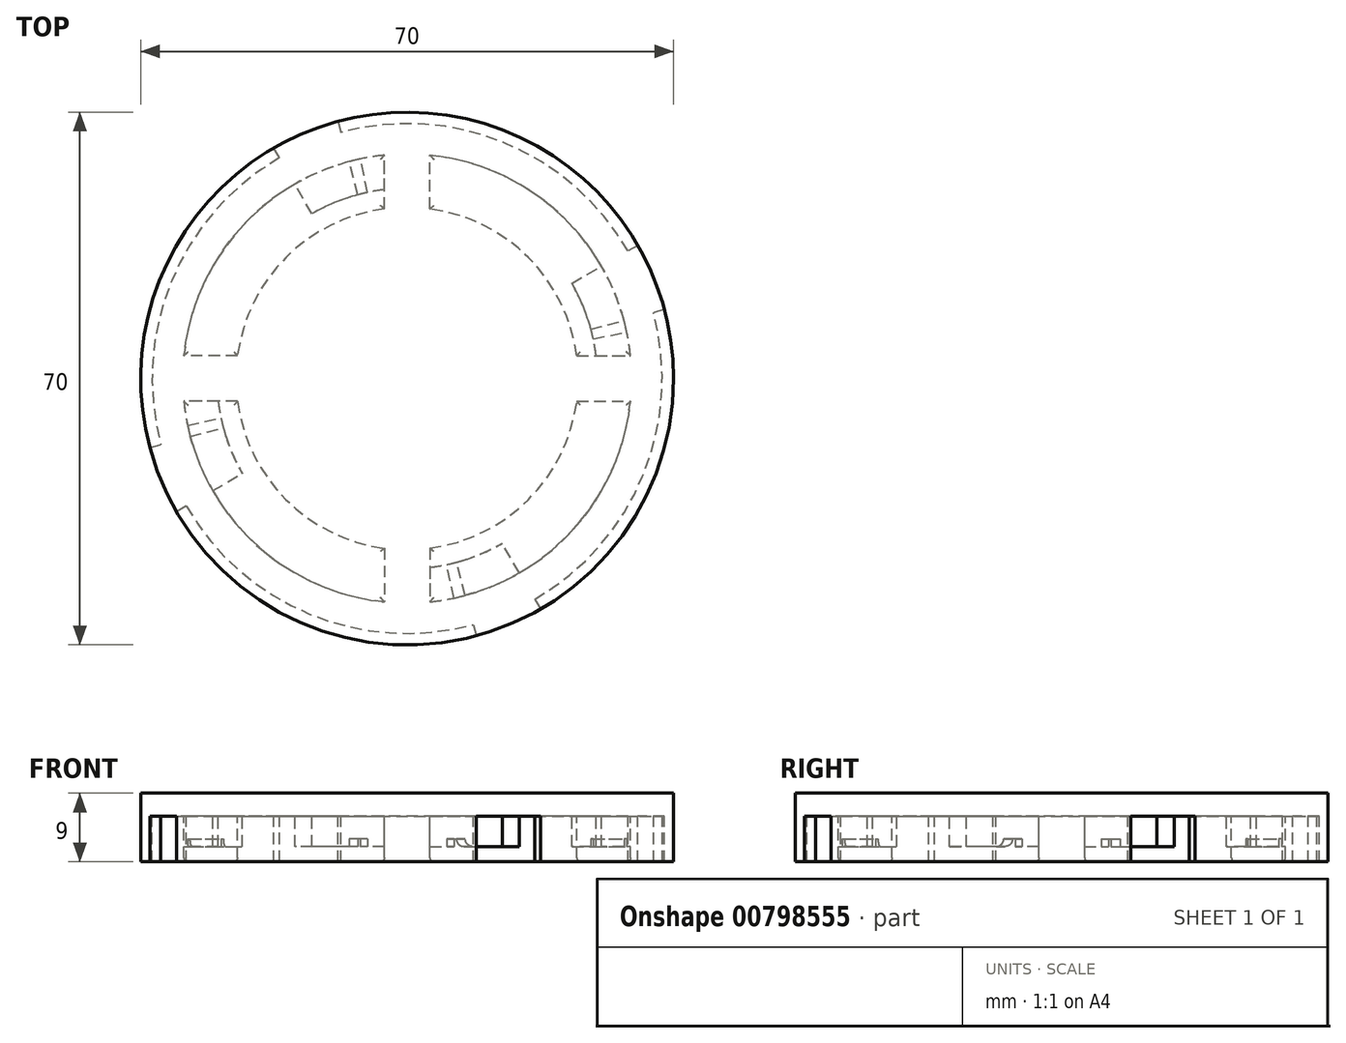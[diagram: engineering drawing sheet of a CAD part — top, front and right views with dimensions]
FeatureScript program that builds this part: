
annotation { "Feature Type Name" : "Feature", "Feature Type Description" : "" }
export const myFeature = defineFeature(function(context is Context, id is Id, definition is map)
    precondition{}
    {
        {
            var Q0;
            Q0=qCreatedBy(makeId("Top.planeOp"),FACE);
            var sketch = newSketch(context, id + "F0", { "sketchPlane" : qUnion([Q0])});
            skCircle(sketch, "E0", {"center": v(0, 0) * mm, "radius": 35 * mm});
            skCircle(sketch, "E1", {"center": v(0, 0) * mm, "radius": 29.5 * mm});
            skCircle(sketch, "E2", {"center": v(0, 0) * mm, "radius": 31 * mm});
            skCircle(sketch, "E3", {"center": v(0, 0) * mm, "radius": 33.5 * mm});
            skCircle(sketch, "E4", {"center": v(0, 0) * mm, "radius": 22.5 * mm});
            skLineSegment(sketch, "E5.bottom", {"start": v(-22.5, 3) * mm, "end": v(-29.5, 3) * mm});
            skLineSegment(sketch, "E5.top", {"start": v(-22.5, -3) * mm, "end": v(-29.5, -3) * mm});
            skLineSegment(sketch, "E5.left", {"start": v(-22.5, 3) * mm, "end": v(-22.5, -3) * mm});
            skLineSegment(sketch, "E5.right", {"start": v(-29.5, 3) * mm, "end": v(-29.5, -3) * mm});
            skPoint(sketch, "E5.middle", {"position": v(-26, 0) * mm});
            skLineSegment(sketch, "E6.bottom", {"start": v(-22.5, -3) * mm, "end": v(-21.5, -3) * mm});
            skLineSegment(sketch, "E6.top", {"start": v(-22.5, 3) * mm, "end": v(-21.5, 3) * mm});
            skLineSegment(sketch, "E6.left", {"start": v(-22.5, -3) * mm, "end": v(-22.5, 3) * mm});
            skLineSegment(sketch, "E6.right", {"start": v(-21.5, -3) * mm, "end": v(-21.5, 3) * mm});
            skPoint(sketch, "E6.middle", {"position": v(-22, 0) * mm});
            skLineSegment(sketch, "E7", {"start": v(-30.31, -17.5) * mm, "end": v(30.31, 17.5) * mm});
            skLineSegment(sketch, "E8", {"start": v(0, -35) * mm, "end": v(0, 35) * mm});
            skLineSegment(sketch, "E9.MirrorCS", {"start": v(21.5, -3) * mm, "end": v(21.5, 3) * mm});
            skLineSegment(sketch, "E10.MirrorCS", {"start": v(22.5, -3) * mm, "end": v(21.5, -3) * mm});
            skLineSegment(sketch, "E11.MirrorCS", {"start": v(22.5, -3) * mm, "end": v(29.5, -3) * mm});
            skLineSegment(sketch, "E12.MirrorCS", {"start": v(29.5, 3) * mm, "end": v(29.5, -3) * mm});
            skLineSegment(sketch, "E13.MirrorCS", {"start": v(22.5, 3) * mm, "end": v(29.5, 3) * mm});
            skLineSegment(sketch, "E14.MirrorCS", {"start": v(22.5, -3) * mm, "end": v(22.5, 3) * mm});
            skLineSegment(sketch, "E15.MirrorCS", {"start": v(22.5, 3) * mm, "end": v(21.5, 3) * mm});
            skLineSegment(sketch, "E16.bottom", {"start": v(3, -22.5) * mm, "end": v(-3, -22.5) * mm});
            skLineSegment(sketch, "E16.top", {"start": v(3, -29.5) * mm, "end": v(-3, -29.5) * mm});
            skLineSegment(sketch, "E16.left", {"start": v(3, -22.5) * mm, "end": v(3, -29.5) * mm});
            skLineSegment(sketch, "E16.right", {"start": v(-3, -22.5) * mm, "end": v(-3, -29.5) * mm});
            skPoint(sketch, "E16.middle", {"position": v(0, -26) * mm});
            skLineSegment(sketch, "E17.bottom", {"start": v(3, -21.5) * mm, "end": v(-3, -21.5) * mm});
            skLineSegment(sketch, "E17.left", {"start": v(3, -21.5) * mm, "end": v(3, -22.5) * mm});
            skLineSegment(sketch, "E17.right", {"start": v(-3, -21.5) * mm, "end": v(-3, -22.5) * mm});
            skPoint(sketch, "E17.middle", {"position": v(0, -22) * mm});
            skLineSegment(sketch, "E18", {"start": v(17.5, -30.31) * mm, "end": v(-17.5, 30.31) * mm});
            skLineSegment(sketch, "E19.bottom", {"start": v(3, 22.5) * mm, "end": v(-3, 22.5) * mm});
            skLineSegment(sketch, "E19.top", {"start": v(3, 29.5) * mm, "end": v(-3, 29.5) * mm});
            skLineSegment(sketch, "E19.left", {"start": v(3, 22.5) * mm, "end": v(3, 29.5) * mm});
            skLineSegment(sketch, "E19.right", {"start": v(-3, 22.5) * mm, "end": v(-3, 29.5) * mm});
            skPoint(sketch, "E19.middle", {"position": v(0, 26) * mm});
            skLineSegment(sketch, "E20.bottom", {"start": v(3, 21.5) * mm, "end": v(-3, 21.5) * mm});
            skLineSegment(sketch, "E20.left", {"start": v(3, 21.5) * mm, "end": v(3, 22.5) * mm});
            skLineSegment(sketch, "E20.right", {"start": v(-3, 21.5) * mm, "end": v(-3, 22.5) * mm});
            skPoint(sketch, "E20.middle", {"position": v(0, 22) * mm});
            skPoint(sketch, "E20.middle.positionSnap0", {"position": v(0, 29.5) * mm});
            skPoint(sketch, "E20.centerSnap0", {"position": v(0, 29.5) * mm});
            skCircle(sketch, "E21", {"center": v(0, 0) * mm, "radius": 25 * mm});
            skLineSegment(sketch, "E22", {"start": v(-35, 0) * mm, "end": v(35, 0) * mm});
            skPoint(sketch, "E23.startSnap0", {"position": v(3, -22) * mm});
            skLineSegment(sketch, "E24", {"start": v(9.06, -33.8) * mm, "end": v(-9.06, 33.8) * mm});
            skLineSegment(sketch, "E25", {"start": v(7.28, -34.24) * mm, "end": v(-7.28, 34.24) * mm});
            skLineSegment(sketch, "E26", {"start": v(-34.24, -7.28) * mm, "end": v(34.24, 7.28) * mm});
            skLineSegment(sketch, "E27", {"start": v(-33.8, -9.06) * mm, "end": v(33.8, 9.06) * mm});
            skSolve(sketch);
        }
        {
            var Q0;
            {var subQ0=sQuery(id+"F0.wireOp",EDGE,"E22");var subQ1=sQuery(id+"F0.wireOp",EDGE,"E0");var subQ2=makeQuery(id+"F0.imprint","INTERSECT",VERTEX,{"disambiguationData":[OD(1.0)],"derivedFrom":[subQ1,subQ0]});Q0=makeQuery(id+"F0.imprint","IMPRINT",FACE,{"disambiguationData":[TD([[makeQuery(id+"F0.imprint","IMPRINT",EDGE,{"disambiguationData":[TD([[subQ2,-1.0]])],"derivedFrom":subQ1}),1.0]])]});}
            var Q1;
            {var subQ0=sQuery(id+"F0.wireOp",EDGE,"E26");var subQ1=sQuery(id+"F0.wireOp",EDGE,"E0");var subQ2=makeQuery(id+"F0.imprint","INTERSECT",VERTEX,{"disambiguationData":[OD(1.0)],"derivedFrom":[subQ1,subQ0]});Q1=makeQuery(id+"F0.imprint","IMPRINT",FACE,{"disambiguationData":[TD([[makeQuery(id+"F0.imprint","IMPRINT",EDGE,{"disambiguationData":[TD([[subQ2,-1.0]])],"derivedFrom":subQ1}),1.0]])]});}
            var Q2;
            {var subQ0=sQuery(id+"F0.wireOp",EDGE,"E7");var subQ1=sQuery(id+"F0.wireOp",EDGE,"E0");var subQ2=makeQuery(id+"F0.imprint","INTERSECT",VERTEX,{"disambiguationData":[OD(1.0)],"derivedFrom":[subQ1,subQ0]});Q2=makeQuery(id+"F0.imprint","IMPRINT",FACE,{"disambiguationData":[TD([[makeQuery(id+"F0.imprint","IMPRINT",EDGE,{"disambiguationData":[TD([[subQ2,1.0]])],"derivedFrom":subQ1}),1.0]])]});}
            var Q3;
            {var subQ0=sQuery(id+"F0.wireOp",EDGE,"E7");var subQ1=sQuery(id+"F0.wireOp",EDGE,"E0");var subQ2=makeQuery(id+"F0.imprint","INTERSECT",VERTEX,{"disambiguationData":[OD(1.0)],"derivedFrom":[subQ1,subQ0]});Q3=makeQuery(id+"F0.imprint","IMPRINT",FACE,{"disambiguationData":[TD([[makeQuery(id+"F0.imprint","IMPRINT",EDGE,{"disambiguationData":[TD([[subQ2,-1.0]])],"derivedFrom":subQ1}),1.0]])]});}
            var Q4;
            {var subQ0=sQuery(id+"F0.wireOp",EDGE,"E8");var subQ1=sQuery(id+"F0.wireOp",EDGE,"E0");var subQ2=makeQuery(id+"F0.imprint","INTERSECT",VERTEX,{"disambiguationData":[OD(1.0)],"derivedFrom":[subQ1,subQ0]});Q4=makeQuery(id+"F0.imprint","IMPRINT",FACE,{"disambiguationData":[TD([[makeQuery(id+"F0.imprint","IMPRINT",EDGE,{"disambiguationData":[TD([[subQ2,-1.0]])],"derivedFrom":subQ1}),1.0]])]});}
            var Q5;
            {var subQ0=sQuery(id+"F0.wireOp",EDGE,"E24");var subQ1=sQuery(id+"F0.wireOp",EDGE,"E0");var subQ2=makeQuery(id+"F0.imprint","INTERSECT",VERTEX,{"disambiguationData":[OD(1.0)],"derivedFrom":[subQ1,subQ0]});Q5=makeQuery(id+"F0.imprint","IMPRINT",FACE,{"disambiguationData":[TD([[makeQuery(id+"F0.imprint","IMPRINT",EDGE,{"disambiguationData":[TD([[subQ2,1.0]])],"derivedFrom":subQ1}),1.0]])]});}
            var Q6;
            {var subQ0=sQuery(id+"F0.wireOp",EDGE,"E18");var subQ1=sQuery(id+"F0.wireOp",EDGE,"E0");var subQ2=makeQuery(id+"F0.imprint","INTERSECT",VERTEX,{"disambiguationData":[OD(1.0)],"derivedFrom":[subQ1,subQ0]});Q6=makeQuery(id+"F0.imprint","IMPRINT",FACE,{"disambiguationData":[TD([[makeQuery(id+"F0.imprint","IMPRINT",EDGE,{"disambiguationData":[TD([[subQ2,1.0]])],"derivedFrom":subQ1}),1.0]])]});}
            var Q7;
            {var subQ0=sQuery(id+"F0.wireOp",EDGE,"E18");var subQ1=sQuery(id+"F0.wireOp",EDGE,"E0");var subQ2=makeQuery(id+"F0.imprint","INTERSECT",VERTEX,{"disambiguationData":[OD(1.0)],"derivedFrom":[subQ1,subQ0]});Q7=makeQuery(id+"F0.imprint","IMPRINT",FACE,{"disambiguationData":[TD([[makeQuery(id+"F0.imprint","IMPRINT",EDGE,{"disambiguationData":[TD([[subQ2,-1.0]])],"derivedFrom":subQ1}),1.0]])]});}
            var Q8;
            {var subQ0=sQuery(id+"F0.wireOp",EDGE,"E22");var subQ1=sQuery(id+"F0.wireOp",EDGE,"E0");var subQ2=makeQuery(id+"F0.imprint","INTERSECT",VERTEX,{"disambiguationData":[OD(0.0)],"derivedFrom":[subQ1,subQ0]});Q8=makeQuery(id+"F0.imprint","IMPRINT",FACE,{"disambiguationData":[TD([[makeQuery(id+"F0.imprint","IMPRINT",EDGE,{"disambiguationData":[TD([[subQ2,-1.0]])],"derivedFrom":subQ1}),1.0]])]});}
            var Q9;
            {var subQ0=sQuery(id+"F0.wireOp",EDGE,"E26");var subQ1=sQuery(id+"F0.wireOp",EDGE,"E0");var subQ2=makeQuery(id+"F0.imprint","INTERSECT",VERTEX,{"disambiguationData":[OD(0.0)],"derivedFrom":[subQ1,subQ0]});Q9=makeQuery(id+"F0.imprint","IMPRINT",FACE,{"disambiguationData":[TD([[makeQuery(id+"F0.imprint","IMPRINT",EDGE,{"disambiguationData":[TD([[subQ2,-1.0]])],"derivedFrom":subQ1}),1.0]])]});}
            var Q10;
            {var subQ0=sQuery(id+"F0.wireOp",EDGE,"E7");var subQ1=sQuery(id+"F0.wireOp",EDGE,"E0");var subQ2=makeQuery(id+"F0.imprint","INTERSECT",VERTEX,{"disambiguationData":[OD(0.0)],"derivedFrom":[subQ1,subQ0]});Q10=makeQuery(id+"F0.imprint","IMPRINT",FACE,{"disambiguationData":[TD([[makeQuery(id+"F0.imprint","IMPRINT",EDGE,{"disambiguationData":[TD([[subQ2,1.0]])],"derivedFrom":subQ1}),1.0]])]});}
            var Q11;
            {var subQ0=sQuery(id+"F0.wireOp",EDGE,"E7");var subQ1=sQuery(id+"F0.wireOp",EDGE,"E0");var subQ2=makeQuery(id+"F0.imprint","INTERSECT",VERTEX,{"disambiguationData":[OD(0.0)],"derivedFrom":[subQ1,subQ0]});Q11=makeQuery(id+"F0.imprint","IMPRINT",FACE,{"disambiguationData":[TD([[makeQuery(id+"F0.imprint","IMPRINT",EDGE,{"disambiguationData":[TD([[subQ2,-1.0]])],"derivedFrom":subQ1}),1.0]])]});}
            var Q12;
            {var subQ0=sQuery(id+"F0.wireOp",EDGE,"E8");var subQ1=sQuery(id+"F0.wireOp",EDGE,"E0");var subQ2=makeQuery(id+"F0.imprint","INTERSECT",VERTEX,{"disambiguationData":[OD(0.0)],"derivedFrom":[subQ1,subQ0]});Q12=makeQuery(id+"F0.imprint","IMPRINT",FACE,{"disambiguationData":[TD([[makeQuery(id+"F0.imprint","IMPRINT",EDGE,{"disambiguationData":[TD([[subQ2,-1.0]])],"derivedFrom":subQ1}),1.0]])]});}
            var Q13;
            {var subQ0=sQuery(id+"F0.wireOp",EDGE,"E24");var subQ1=sQuery(id+"F0.wireOp",EDGE,"E0");var subQ2=makeQuery(id+"F0.imprint","INTERSECT",VERTEX,{"disambiguationData":[OD(0.0)],"derivedFrom":[subQ1,subQ0]});Q13=makeQuery(id+"F0.imprint","IMPRINT",FACE,{"disambiguationData":[TD([[makeQuery(id+"F0.imprint","IMPRINT",EDGE,{"disambiguationData":[TD([[subQ2,1.0]])],"derivedFrom":subQ1}),1.0]])]});}
            var Q14;
            {var subQ0=sQuery(id+"F0.wireOp",EDGE,"E18");var subQ1=sQuery(id+"F0.wireOp",EDGE,"E0");var subQ2=makeQuery(id+"F0.imprint","INTERSECT",VERTEX,{"disambiguationData":[OD(0.0)],"derivedFrom":[subQ1,subQ0]});Q14=makeQuery(id+"F0.imprint","IMPRINT",FACE,{"disambiguationData":[TD([[makeQuery(id+"F0.imprint","IMPRINT",EDGE,{"disambiguationData":[TD([[subQ2,1.0]])],"derivedFrom":subQ1}),1.0]])]});}
            var Q15;
            {var subQ0=sQuery(id+"F0.wireOp",EDGE,"E18");var subQ1=sQuery(id+"F0.wireOp",EDGE,"E0");var subQ2=makeQuery(id+"F0.imprint","INTERSECT",VERTEX,{"disambiguationData":[OD(0.0)],"derivedFrom":[subQ1,subQ0]});Q15=makeQuery(id+"F0.imprint","IMPRINT",FACE,{"disambiguationData":[TD([[makeQuery(id+"F0.imprint","IMPRINT",EDGE,{"disambiguationData":[TD([[subQ2,-1.0]])],"derivedFrom":subQ1}),1.0]])]});}
            var Q16;
            {var subQ0=sQuery(id+"F0.wireOp",EDGE,"E18");var subQ1=sQuery(id+"F0.wireOp",EDGE,"E4");var subQ2=makeQuery(id+"F0.imprint","INTERSECT",VERTEX,{"disambiguationData":[OD(0.0)],"derivedFrom":[subQ1,subQ0]});Q16=makeQuery(id+"F0.imprint","IMPRINT",FACE,{"disambiguationData":[TD([[makeQuery(id+"F0.imprint","IMPRINT",EDGE,{"disambiguationData":[TD([[subQ2,-1.0]])],"derivedFrom":subQ1}),1.0]])]});}
            var Q17;
            {var subQ5=sQuery(id+"F0.wireOp",EDGE,"E6.bottom");var subQ6=sQuery(id+"F0.wireOp",EDGE,"E4");var subQ7=makeQuery(id+"F0.imprint","INTERSECT",VERTEX,{"derivedFrom":[subQ6,subQ5]});Q17=makeQuery(id+"F0.imprint","IMPRINT",FACE,{"disambiguationData":[TD([[makeQuery(id+"F0.imprint","IMPRINT",EDGE,{"disambiguationData":[TD([[subQ7,-1.0]])],"derivedFrom":subQ6}),1.0]])]});}
            var Q18;
            {var subQ0=sQuery(id+"F0.wireOp",EDGE,"E26");var subQ1=sQuery(id+"F0.wireOp",EDGE,"E2");var subQ2=makeQuery(id+"F0.imprint","INTERSECT",VERTEX,{"disambiguationData":[OD(0.0)],"derivedFrom":[subQ1,subQ0]});Q18=makeQuery(id+"F0.imprint","IMPRINT",FACE,{"disambiguationData":[TD([[makeQuery(id+"F0.imprint","IMPRINT",EDGE,{"disambiguationData":[TD([[subQ2,1.0]])],"derivedFrom":subQ1}),-1.0]])]});}
            var Q19;
            {var subQ0=sQuery(id+"F0.wireOp",EDGE,"E26");var subQ1=sQuery(id+"F0.wireOp",EDGE,"E2");var subQ2=makeQuery(id+"F0.imprint","INTERSECT",VERTEX,{"disambiguationData":[OD(0.0)],"derivedFrom":[subQ1,subQ0]});Q19=makeQuery(id+"F0.imprint","IMPRINT",FACE,{"disambiguationData":[TD([[makeQuery(id+"F0.imprint","IMPRINT",EDGE,{"disambiguationData":[TD([[subQ2,-1.0]])],"derivedFrom":subQ1}),-1.0]])]});}
            var Q20;
            {var subQ0=sQuery(id+"F0.wireOp",EDGE,"E27");var subQ1=sQuery(id+"F0.wireOp",EDGE,"E2");var subQ2=makeQuery(id+"F0.imprint","INTERSECT",VERTEX,{"disambiguationData":[OD(0.0)],"derivedFrom":[subQ1,subQ0]});Q20=makeQuery(id+"F0.imprint","IMPRINT",FACE,{"disambiguationData":[TD([[makeQuery(id+"F0.imprint","IMPRINT",EDGE,{"disambiguationData":[TD([[subQ2,-1.0]])],"derivedFrom":subQ1}),-1.0]])]});}
            var Q21;
            {var subQ0=sQuery(id+"F0.wireOp",EDGE,"E7");var subQ1=sQuery(id+"F0.wireOp",EDGE,"E2");var subQ2=makeQuery(id+"F0.imprint","INTERSECT",VERTEX,{"disambiguationData":[OD(0.0)],"derivedFrom":[subQ1,subQ0]});Q21=makeQuery(id+"F0.imprint","IMPRINT",FACE,{"disambiguationData":[TD([[makeQuery(id+"F0.imprint","IMPRINT",EDGE,{"disambiguationData":[TD([[subQ2,-1.0]])],"derivedFrom":subQ1}),-1.0]])]});}
            var Q22;
            {var subQ0=sQuery(id+"F0.wireOp",EDGE,"E8");var subQ1=sQuery(id+"F0.wireOp",EDGE,"E2");var subQ2=makeQuery(id+"F0.imprint","INTERSECT",VERTEX,{"disambiguationData":[OD(0.0)],"derivedFrom":[subQ1,subQ0]});Q22=makeQuery(id+"F0.imprint","IMPRINT",FACE,{"disambiguationData":[TD([[makeQuery(id+"F0.imprint","IMPRINT",EDGE,{"disambiguationData":[TD([[subQ2,-1.0]])],"derivedFrom":subQ1}),-1.0]])]});}
            var Q23;
            {var subQ0=sQuery(id+"F0.wireOp",EDGE,"E25");var subQ1=sQuery(id+"F0.wireOp",EDGE,"E2");var subQ2=makeQuery(id+"F0.imprint","INTERSECT",VERTEX,{"disambiguationData":[OD(0.0)],"derivedFrom":[subQ1,subQ0]});Q23=makeQuery(id+"F0.imprint","IMPRINT",FACE,{"disambiguationData":[TD([[makeQuery(id+"F0.imprint","IMPRINT",EDGE,{"disambiguationData":[TD([[subQ2,-1.0]])],"derivedFrom":subQ1}),-1.0]])]});}
            var Q24;
            {var subQ0=sQuery(id+"F0.wireOp",EDGE,"E24");var subQ1=sQuery(id+"F0.wireOp",EDGE,"E2");var subQ2=makeQuery(id+"F0.imprint","INTERSECT",VERTEX,{"disambiguationData":[OD(0.0)],"derivedFrom":[subQ1,subQ0]});Q24=makeQuery(id+"F0.imprint","IMPRINT",FACE,{"disambiguationData":[TD([[makeQuery(id+"F0.imprint","IMPRINT",EDGE,{"disambiguationData":[TD([[subQ2,-1.0]])],"derivedFrom":subQ1}),-1.0]])]});}
            var Q25;
            {var subQ0=sQuery(id+"F0.wireOp",EDGE,"E18");var subQ1=sQuery(id+"F0.wireOp",EDGE,"E2");var subQ2=makeQuery(id+"F0.imprint","INTERSECT",VERTEX,{"disambiguationData":[OD(0.0)],"derivedFrom":[subQ1,subQ0]});Q25=makeQuery(id+"F0.imprint","IMPRINT",FACE,{"disambiguationData":[TD([[makeQuery(id+"F0.imprint","IMPRINT",EDGE,{"disambiguationData":[TD([[subQ2,-1.0]])],"derivedFrom":subQ1}),-1.0]])]});}
            var Q26;
            {var subQ0=sQuery(id+"F0.wireOp",EDGE,"E22");var subQ1=sQuery(id+"F0.wireOp",EDGE,"E2");var subQ2=makeQuery(id+"F0.imprint","INTERSECT",VERTEX,{"disambiguationData":[OD(1.0)],"derivedFrom":[subQ1,subQ0]});Q26=makeQuery(id+"F0.imprint","IMPRINT",FACE,{"disambiguationData":[TD([[makeQuery(id+"F0.imprint","IMPRINT",EDGE,{"disambiguationData":[TD([[subQ2,-1.0]])],"derivedFrom":subQ1}),-1.0]])]});}
            var Q27;
            {var subQ0=sQuery(id+"F0.wireOp",EDGE,"E26");var subQ1=sQuery(id+"F0.wireOp",EDGE,"E2");var subQ2=makeQuery(id+"F0.imprint","INTERSECT",VERTEX,{"disambiguationData":[OD(1.0)],"derivedFrom":[subQ1,subQ0]});Q27=makeQuery(id+"F0.imprint","IMPRINT",FACE,{"disambiguationData":[TD([[makeQuery(id+"F0.imprint","IMPRINT",EDGE,{"disambiguationData":[TD([[subQ2,-1.0]])],"derivedFrom":subQ1}),-1.0]])]});}
            var Q28;
            {var subQ0=sQuery(id+"F0.wireOp",EDGE,"E27");var subQ1=sQuery(id+"F0.wireOp",EDGE,"E2");var subQ2=makeQuery(id+"F0.imprint","INTERSECT",VERTEX,{"disambiguationData":[OD(1.0)],"derivedFrom":[subQ1,subQ0]});Q28=makeQuery(id+"F0.imprint","IMPRINT",FACE,{"disambiguationData":[TD([[makeQuery(id+"F0.imprint","IMPRINT",EDGE,{"disambiguationData":[TD([[subQ2,-1.0]])],"derivedFrom":subQ1}),-1.0]])]});}
            var Q29;
            {var subQ0=sQuery(id+"F0.wireOp",EDGE,"E7");var subQ1=sQuery(id+"F0.wireOp",EDGE,"E2");var subQ2=makeQuery(id+"F0.imprint","INTERSECT",VERTEX,{"disambiguationData":[OD(1.0)],"derivedFrom":[subQ1,subQ0]});Q29=makeQuery(id+"F0.imprint","IMPRINT",FACE,{"disambiguationData":[TD([[makeQuery(id+"F0.imprint","IMPRINT",EDGE,{"disambiguationData":[TD([[subQ2,-1.0]])],"derivedFrom":subQ1}),-1.0]])]});}
            var Q30;
            {var subQ0=sQuery(id+"F0.wireOp",EDGE,"E8");var subQ1=sQuery(id+"F0.wireOp",EDGE,"E2");var subQ2=makeQuery(id+"F0.imprint","INTERSECT",VERTEX,{"disambiguationData":[OD(1.0)],"derivedFrom":[subQ1,subQ0]});Q30=makeQuery(id+"F0.imprint","IMPRINT",FACE,{"disambiguationData":[TD([[makeQuery(id+"F0.imprint","IMPRINT",EDGE,{"disambiguationData":[TD([[subQ2,-1.0]])],"derivedFrom":subQ1}),-1.0]])]});}
            var Q31;
            {var subQ0=sQuery(id+"F0.wireOp",EDGE,"E25");var subQ1=sQuery(id+"F0.wireOp",EDGE,"E2");var subQ2=makeQuery(id+"F0.imprint","INTERSECT",VERTEX,{"disambiguationData":[OD(1.0)],"derivedFrom":[subQ1,subQ0]});Q31=makeQuery(id+"F0.imprint","IMPRINT",FACE,{"disambiguationData":[TD([[makeQuery(id+"F0.imprint","IMPRINT",EDGE,{"disambiguationData":[TD([[subQ2,-1.0]])],"derivedFrom":subQ1}),-1.0]])]});}
            var Q32;
            {var subQ0=sQuery(id+"F0.wireOp",EDGE,"E24");var subQ1=sQuery(id+"F0.wireOp",EDGE,"E2");var subQ2=makeQuery(id+"F0.imprint","INTERSECT",VERTEX,{"disambiguationData":[OD(1.0)],"derivedFrom":[subQ1,subQ0]});Q32=makeQuery(id+"F0.imprint","IMPRINT",FACE,{"disambiguationData":[TD([[makeQuery(id+"F0.imprint","IMPRINT",EDGE,{"disambiguationData":[TD([[subQ2,-1.0]])],"derivedFrom":subQ1}),-1.0]])]});}
            var Q33;
            {var subQ0=sQuery(id+"F0.wireOp",EDGE,"E22");var subQ1=sQuery(id+"F0.wireOp",EDGE,"E2");var subQ2=makeQuery(id+"F0.imprint","INTERSECT",VERTEX,{"disambiguationData":[OD(0.0)],"derivedFrom":[subQ1,subQ0]});Q33=makeQuery(id+"F0.imprint","IMPRINT",FACE,{"disambiguationData":[TD([[makeQuery(id+"F0.imprint","IMPRINT",EDGE,{"disambiguationData":[TD([[subQ2,1.0]])],"derivedFrom":subQ1}),-1.0]])]});}
            var Q34;
            {var subQ0=sQuery(id+"F0.wireOp",EDGE,"E27");var subQ1=sQuery(id+"F0.wireOp",EDGE,"E1");var subQ2=makeQuery(id+"F0.imprint","INTERSECT",VERTEX,{"disambiguationData":[OD(1.0)],"derivedFrom":[subQ1,subQ0]});Q34=makeQuery(id+"F0.imprint","IMPRINT",FACE,{"disambiguationData":[TD([[makeQuery(id+"F0.imprint","IMPRINT",EDGE,{"disambiguationData":[TD([[subQ2,-1.0]])],"derivedFrom":subQ1}),1.0]])]});}
            var Q35;
            {var subQ0=sQuery(id+"F0.wireOp",EDGE,"E15.MirrorCS");var subQ5=sQuery(id+"F0.wireOp",EDGE,"E9.MirrorCS");var subQ6=makeQuery(id+"F0.imprint","INTERSECT",VERTEX,{"derivedFrom":[subQ5,subQ0]});Q35=makeQuery(id+"F0.imprint","IMPRINT",FACE,{"disambiguationData":[TD([[makeQuery(id+"F0.imprint","IMPRINT",EDGE,{"disambiguationData":[TD([[subQ6,1.0]])],"derivedFrom":subQ5}),-1.0]])]});}
            var Q36;
            {var subQ0=sQuery(id+"F0.wireOp",EDGE,"E10.MirrorCS");var subQ5=sQuery(id+"F0.wireOp",EDGE,"E9.MirrorCS");var subQ7=makeQuery(id+"F0.imprint","INTERSECT",VERTEX,{"derivedFrom":[subQ5,subQ0]});Q36=makeQuery(id+"F0.imprint","IMPRINT",FACE,{"disambiguationData":[TD([[makeQuery(id+"F0.imprint","IMPRINT",EDGE,{"disambiguationData":[TD([[subQ7,-1.0]])],"derivedFrom":subQ5}),-1.0]])]});}
            var Q37;
            {var subQ5=sQuery(id+"F0.wireOp",EDGE,"E15.MirrorCS");var subQ7=sQuery(id+"F0.wireOp",EDGE,"E4");var subQ8=makeQuery(id+"F0.imprint","INTERSECT",VERTEX,{"derivedFrom":[subQ7,subQ5]});Q37=makeQuery(id+"F0.imprint","IMPRINT",FACE,{"disambiguationData":[TD([[makeQuery(id+"F0.imprint","IMPRINT",EDGE,{"disambiguationData":[TD([[subQ8,-1.0]])],"derivedFrom":subQ7}),1.0]])]});}
            var Q38;
            {var subQ0=sQuery(id+"F0.wireOp",EDGE,"E18");var subQ1=sQuery(id+"F0.wireOp",EDGE,"E4");var subQ2=makeQuery(id+"F0.imprint","INTERSECT",VERTEX,{"disambiguationData":[OD(1.0)],"derivedFrom":[subQ1,subQ0]});Q38=makeQuery(id+"F0.imprint","IMPRINT",FACE,{"disambiguationData":[TD([[makeQuery(id+"F0.imprint","IMPRINT",EDGE,{"disambiguationData":[TD([[subQ2,-1.0]])],"derivedFrom":subQ1}),1.0]])]});}
            var Q39;
            {var subQ0=sQuery(id+"F0.wireOp",EDGE,"E27");var subQ1=sQuery(id+"F0.wireOp",EDGE,"E1");var subQ2=makeQuery(id+"F0.imprint","INTERSECT",VERTEX,{"disambiguationData":[OD(0.0)],"derivedFrom":[subQ1,subQ0]});Q39=makeQuery(id+"F0.imprint","IMPRINT",FACE,{"disambiguationData":[TD([[makeQuery(id+"F0.imprint","IMPRINT",EDGE,{"disambiguationData":[TD([[subQ2,-1.0]])],"derivedFrom":subQ1}),1.0]])]});}
            var Q40;
            {var subQ0=sQuery(id+"F0.wireOp",EDGE,"E7");var subQ1=sQuery(id+"F0.wireOp",EDGE,"E1");var subQ2=makeQuery(id+"F0.imprint","INTERSECT",VERTEX,{"disambiguationData":[OD(0.0)],"derivedFrom":[subQ1,subQ0]});Q40=makeQuery(id+"F0.imprint","IMPRINT",FACE,{"disambiguationData":[TD([[makeQuery(id+"F0.imprint","IMPRINT",EDGE,{"disambiguationData":[TD([[subQ2,-1.0]])],"derivedFrom":subQ1}),1.0]])]});}
            var Q41;
            {var subQ0=sQuery(id+"F0.wireOp",EDGE,"E13.MirrorCS");var subQ1=sQuery(id+"F0.wireOp",EDGE,"E1");var subQ2=makeQuery(id+"F0.imprint","INTERSECT",VERTEX,{"derivedFrom":[subQ1,subQ0]});Q41=makeQuery(id+"F0.imprint","IMPRINT",FACE,{"disambiguationData":[TD([[makeQuery(id+"F0.imprint","IMPRINT",EDGE,{"disambiguationData":[TD([[subQ2,1.0]])],"derivedFrom":subQ0}),-1.0]])]});}
            var Q42;
            {var subQ0=sQuery(id+"F0.wireOp",EDGE,"E7");var subQ1=sQuery(id+"F0.wireOp",EDGE,"E1");var subQ2=makeQuery(id+"F0.imprint","INTERSECT",VERTEX,{"disambiguationData":[OD(1.0)],"derivedFrom":[subQ1,subQ0]});Q42=makeQuery(id+"F0.imprint","IMPRINT",FACE,{"disambiguationData":[TD([[makeQuery(id+"F0.imprint","IMPRINT",EDGE,{"disambiguationData":[TD([[subQ2,-1.0]])],"derivedFrom":subQ1}),1.0]])]});}
            var Q43;
            {var subQ0=sQuery(id+"F0.wireOp",EDGE,"E26");var subQ1=sQuery(id+"F0.wireOp",EDGE,"E1");var subQ2=makeQuery(id+"F0.imprint","INTERSECT",VERTEX,{"disambiguationData":[OD(0.0)],"derivedFrom":[subQ1,subQ0]});Q43=makeQuery(id+"F0.imprint","IMPRINT",FACE,{"disambiguationData":[TD([[makeQuery(id+"F0.imprint","IMPRINT",EDGE,{"disambiguationData":[TD([[subQ2,-1.0]])],"derivedFrom":subQ1}),-1.0]])]});}
            var Q44;
            {var subQ0=sQuery(id+"F0.wireOp",EDGE,"E27");var subQ1=sQuery(id+"F0.wireOp",EDGE,"E1");var subQ2=makeQuery(id+"F0.imprint","INTERSECT",VERTEX,{"disambiguationData":[OD(0.0)],"derivedFrom":[subQ1,subQ0]});Q44=makeQuery(id+"F0.imprint","IMPRINT",FACE,{"disambiguationData":[TD([[makeQuery(id+"F0.imprint","IMPRINT",EDGE,{"disambiguationData":[TD([[subQ2,-1.0]])],"derivedFrom":subQ1}),-1.0]])]});}
            var Q45;
            {var subQ0=sQuery(id+"F0.wireOp",EDGE,"E25");var subQ1=sQuery(id+"F0.wireOp",EDGE,"E1");var subQ2=makeQuery(id+"F0.imprint","INTERSECT",VERTEX,{"disambiguationData":[OD(0.0)],"derivedFrom":[subQ1,subQ0]});Q45=makeQuery(id+"F0.imprint","IMPRINT",FACE,{"disambiguationData":[TD([[makeQuery(id+"F0.imprint","IMPRINT",EDGE,{"disambiguationData":[TD([[subQ2,-1.0]])],"derivedFrom":subQ1}),-1.0]])]});}
            var Q46;
            {var subQ0=sQuery(id+"F0.wireOp",EDGE,"E24");var subQ1=sQuery(id+"F0.wireOp",EDGE,"E1");var subQ2=makeQuery(id+"F0.imprint","INTERSECT",VERTEX,{"disambiguationData":[OD(0.0)],"derivedFrom":[subQ1,subQ0]});Q46=makeQuery(id+"F0.imprint","IMPRINT",FACE,{"disambiguationData":[TD([[makeQuery(id+"F0.imprint","IMPRINT",EDGE,{"disambiguationData":[TD([[subQ2,-1.0]])],"derivedFrom":subQ1}),-1.0]])]});}
            var Q47;
            {var subQ0=sQuery(id+"F0.wireOp",EDGE,"E26");var subQ1=sQuery(id+"F0.wireOp",EDGE,"E1");var subQ2=makeQuery(id+"F0.imprint","INTERSECT",VERTEX,{"disambiguationData":[OD(1.0)],"derivedFrom":[subQ1,subQ0]});Q47=makeQuery(id+"F0.imprint","IMPRINT",FACE,{"disambiguationData":[TD([[makeQuery(id+"F0.imprint","IMPRINT",EDGE,{"disambiguationData":[TD([[subQ2,-1.0]])],"derivedFrom":subQ1}),-1.0]])]});}
            var Q48;
            {var subQ0=sQuery(id+"F0.wireOp",EDGE,"E27");var subQ1=sQuery(id+"F0.wireOp",EDGE,"E1");var subQ2=makeQuery(id+"F0.imprint","INTERSECT",VERTEX,{"disambiguationData":[OD(1.0)],"derivedFrom":[subQ1,subQ0]});Q48=makeQuery(id+"F0.imprint","IMPRINT",FACE,{"disambiguationData":[TD([[makeQuery(id+"F0.imprint","IMPRINT",EDGE,{"disambiguationData":[TD([[subQ2,-1.0]])],"derivedFrom":subQ1}),-1.0]])]});}
            var Q49;
            {var subQ0=sQuery(id+"F0.wireOp",EDGE,"E25");var subQ1=sQuery(id+"F0.wireOp",EDGE,"E1");var subQ2=makeQuery(id+"F0.imprint","INTERSECT",VERTEX,{"disambiguationData":[OD(1.0)],"derivedFrom":[subQ1,subQ0]});Q49=makeQuery(id+"F0.imprint","IMPRINT",FACE,{"disambiguationData":[TD([[makeQuery(id+"F0.imprint","IMPRINT",EDGE,{"disambiguationData":[TD([[subQ2,-1.0]])],"derivedFrom":subQ1}),-1.0]])]});}
            var Q50;
            {var subQ0=sQuery(id+"F0.wireOp",EDGE,"E24");var subQ1=sQuery(id+"F0.wireOp",EDGE,"E1");var subQ2=makeQuery(id+"F0.imprint","INTERSECT",VERTEX,{"disambiguationData":[OD(1.0)],"derivedFrom":[subQ1,subQ0]});Q50=makeQuery(id+"F0.imprint","IMPRINT",FACE,{"disambiguationData":[TD([[makeQuery(id+"F0.imprint","IMPRINT",EDGE,{"disambiguationData":[TD([[subQ2,-1.0]])],"derivedFrom":subQ1}),-1.0]])]});}
            var Q51;
            {var subQ0=sQuery(id+"F0.wireOp",EDGE,"E13.MirrorCS");var subQ3=sQuery(id+"F0.wireOp",EDGE,"E12.MirrorCS");var subQ5=makeQuery(id+"F0.imprint","INTERSECT",VERTEX,{"derivedFrom":[subQ3,subQ0]});Q51=makeQuery(id+"F0.imprint","IMPRINT",FACE,{"disambiguationData":[TD([[makeQuery(id+"F0.imprint","IMPRINT",EDGE,{"disambiguationData":[TD([[subQ5,1.0]])],"derivedFrom":subQ0}),-1.0]])]});}
            var Q52;
            {var subQ0=sQuery(id+"F0.wireOp",EDGE,"E6.top");var subQ5=sQuery(id+"F0.wireOp",EDGE,"E6.right");var subQ6=makeQuery(id+"F0.imprint","INTERSECT",VERTEX,{"derivedFrom":[subQ0,subQ5]});Q52=makeQuery(id+"F0.imprint","IMPRINT",FACE,{"disambiguationData":[TD([[makeQuery(id+"F0.imprint","IMPRINT",EDGE,{"disambiguationData":[TD([[subQ6,1.0]])],"derivedFrom":subQ0}),-1.0]])]});}
            var Q53;
            {var subQ0=sQuery(id+"F0.wireOp",EDGE,"E6.bottom");var subQ5=sQuery(id+"F0.wireOp",EDGE,"E6.right");var subQ6=makeQuery(id+"F0.imprint","INTERSECT",VERTEX,{"derivedFrom":[subQ0,subQ5]});Q53=makeQuery(id+"F0.imprint","IMPRINT",FACE,{"disambiguationData":[TD([[makeQuery(id+"F0.imprint","IMPRINT",EDGE,{"disambiguationData":[TD([[subQ6,1.0]])],"derivedFrom":subQ0}),1.0]])]});}
            var Q54;
            {var subQ0=sQuery(id+"F0.wireOp",EDGE,"E5.bottom");var subQ1=sQuery(id+"F0.wireOp",EDGE,"E1");var subQ2=makeQuery(id+"F0.imprint","INTERSECT",VERTEX,{"derivedFrom":[subQ1,subQ0]});Q54=makeQuery(id+"F0.imprint","IMPRINT",FACE,{"disambiguationData":[TD([[makeQuery(id+"F0.imprint","IMPRINT",EDGE,{"disambiguationData":[TD([[subQ2,1.0]])],"derivedFrom":subQ0}),1.0]])]});}
            var Q55;
            {var subQ0=sQuery(id+"F0.wireOp",EDGE,"E11.MirrorCS");var subQ3=sQuery(id+"F0.wireOp",EDGE,"E12.MirrorCS");var subQ5=makeQuery(id+"F0.imprint","INTERSECT",VERTEX,{"derivedFrom":[subQ0,subQ3]});Q55=makeQuery(id+"F0.imprint","IMPRINT",FACE,{"disambiguationData":[TD([[makeQuery(id+"F0.imprint","IMPRINT",EDGE,{"disambiguationData":[TD([[subQ5,1.0]])],"derivedFrom":subQ0}),1.0]])]});}
            var Q56;
            {var subQ0=sQuery(id+"F0.wireOp",EDGE,"E15.MirrorCS");var subQ1=sQuery(id+"F0.wireOp",EDGE,"E4");var subQ2=makeQuery(id+"F0.imprint","INTERSECT",VERTEX,{"derivedFrom":[subQ1,subQ0]});Q56=makeQuery(id+"F0.imprint","IMPRINT",FACE,{"disambiguationData":[TD([[makeQuery(id+"F0.imprint","IMPRINT",EDGE,{"disambiguationData":[TD([[subQ2,1.0]])],"derivedFrom":subQ1}),-1.0]])]});}
            var Q57;
            {var subQ0=sQuery(id+"F0.wireOp",EDGE,"E10.MirrorCS");var subQ1=sQuery(id+"F0.wireOp",EDGE,"E4");var subQ2=makeQuery(id+"F0.imprint","INTERSECT",VERTEX,{"derivedFrom":[subQ1,subQ0]});Q57=makeQuery(id+"F0.imprint","IMPRINT",FACE,{"disambiguationData":[TD([[makeQuery(id+"F0.imprint","IMPRINT",EDGE,{"disambiguationData":[TD([[subQ2,-1.0]])],"derivedFrom":subQ1}),-1.0]])]});}
            var Q58;
            {var subQ0=sQuery(id+"F0.wireOp",EDGE,"E5.bottom");var subQ3=sQuery(id+"F0.wireOp",EDGE,"E5.right");var subQ5=makeQuery(id+"F0.imprint","INTERSECT",VERTEX,{"derivedFrom":[subQ0,subQ3]});Q58=makeQuery(id+"F0.imprint","IMPRINT",FACE,{"disambiguationData":[TD([[makeQuery(id+"F0.imprint","IMPRINT",EDGE,{"disambiguationData":[TD([[subQ5,1.0]])],"derivedFrom":subQ0}),1.0]])]});}
            var Q59;
            {var subQ0=sQuery(id+"F0.wireOp",EDGE,"E6.bottom");var subQ1=sQuery(id+"F0.wireOp",EDGE,"E4");var subQ2=makeQuery(id+"F0.imprint","INTERSECT",VERTEX,{"derivedFrom":[subQ1,subQ0]});Q59=makeQuery(id+"F0.imprint","IMPRINT",FACE,{"disambiguationData":[TD([[makeQuery(id+"F0.imprint","IMPRINT",EDGE,{"disambiguationData":[TD([[subQ2,1.0]])],"derivedFrom":subQ1}),-1.0]])]});}
            var Q60;
            {var subQ0=sQuery(id+"F0.wireOp",EDGE,"E5.top");var subQ3=sQuery(id+"F0.wireOp",EDGE,"E5.right");var subQ5=makeQuery(id+"F0.imprint","INTERSECT",VERTEX,{"derivedFrom":[subQ0,subQ3]});Q60=makeQuery(id+"F0.imprint","IMPRINT",FACE,{"disambiguationData":[TD([[makeQuery(id+"F0.imprint","IMPRINT",EDGE,{"disambiguationData":[TD([[subQ5,1.0]])],"derivedFrom":subQ0}),-1.0]])]});}
            var Q61;
            {var subQ0=sQuery(id+"F0.wireOp",EDGE,"E6.top");var subQ1=sQuery(id+"F0.wireOp",EDGE,"E4");var subQ2=makeQuery(id+"F0.imprint","INTERSECT",VERTEX,{"derivedFrom":[subQ1,subQ0]});Q61=makeQuery(id+"F0.imprint","IMPRINT",FACE,{"disambiguationData":[TD([[makeQuery(id+"F0.imprint","IMPRINT",EDGE,{"disambiguationData":[TD([[subQ2,-1.0]])],"derivedFrom":subQ1}),-1.0]])]});}
            var Q62;
            {var subQ5=sQuery(id+"F0.wireOp",EDGE,"E7");var subQ6=sQuery(id+"F0.wireOp",EDGE,"E4");var subQ7=makeQuery(id+"F0.imprint","INTERSECT",VERTEX,{"disambiguationData":[OD(0.0)],"derivedFrom":[subQ6,subQ5]});Q62=makeQuery(id+"F0.imprint","IMPRINT",FACE,{"disambiguationData":[TD([[makeQuery(id+"F0.imprint","IMPRINT",EDGE,{"disambiguationData":[TD([[subQ7,-1.0]])],"derivedFrom":subQ6}),1.0]])]});}
            var Q63;
            {var subQ0=sQuery(id+"F0.wireOp",EDGE,"E20.right");var subQ3=sQuery(id+"F0.wireOp",EDGE,"E4");var subQ4=makeQuery(id+"F0.imprint","INTERSECT",VERTEX,{"derivedFrom":[subQ3,subQ0]});Q63=makeQuery(id+"F0.imprint","IMPRINT",FACE,{"disambiguationData":[TD([[makeQuery(id+"F0.imprint","IMPRINT",EDGE,{"disambiguationData":[TD([[subQ4,-1.0]])],"derivedFrom":subQ3}),1.0]])]});}
            var Q64;
            {var subQ0=sQuery(id+"F0.wireOp",EDGE,"E24");var subQ1=sQuery(id+"F0.wireOp",EDGE,"E1");var subQ2=makeQuery(id+"F0.imprint","INTERSECT",VERTEX,{"disambiguationData":[OD(1.0)],"derivedFrom":[subQ1,subQ0]});Q64=makeQuery(id+"F0.imprint","IMPRINT",FACE,{"disambiguationData":[TD([[makeQuery(id+"F0.imprint","IMPRINT",EDGE,{"disambiguationData":[TD([[subQ2,-1.0]])],"derivedFrom":subQ1}),1.0]])]});}
            var Q65;
            {var subQ0=sQuery(id+"F0.wireOp",EDGE,"E19.left");var subQ1=sQuery(id+"F0.wireOp",EDGE,"E1");var subQ2=makeQuery(id+"F0.imprint","INTERSECT",VERTEX,{"derivedFrom":[subQ1,subQ0]});Q65=makeQuery(id+"F0.imprint","IMPRINT",FACE,{"disambiguationData":[TD([[makeQuery(id+"F0.imprint","IMPRINT",EDGE,{"disambiguationData":[TD([[subQ2,1.0]])],"derivedFrom":subQ0}),1.0]])]});}
            var Q66;
            {var subQ0=sQuery(id+"F0.wireOp",EDGE,"E17.right");var subQ5=sQuery(id+"F0.wireOp",EDGE,"E17.bottom");var subQ7=makeQuery(id+"F0.imprint","INTERSECT",VERTEX,{"derivedFrom":[subQ5,subQ0]});Q66=makeQuery(id+"F0.imprint","IMPRINT",FACE,{"disambiguationData":[TD([[makeQuery(id+"F0.imprint","IMPRINT",EDGE,{"disambiguationData":[TD([[subQ7,1.0]])],"derivedFrom":subQ5}),1.0]])]});}
            var Q67;
            {var subQ0=sQuery(id+"F0.wireOp",EDGE,"E17.left");var subQ5=sQuery(id+"F0.wireOp",EDGE,"E17.bottom");var subQ7=makeQuery(id+"F0.imprint","INTERSECT",VERTEX,{"derivedFrom":[subQ5,subQ0]});Q67=makeQuery(id+"F0.imprint","IMPRINT",FACE,{"disambiguationData":[TD([[makeQuery(id+"F0.imprint","IMPRINT",EDGE,{"disambiguationData":[TD([[subQ7,-1.0]])],"derivedFrom":subQ5}),1.0]])]});}
            var Q68;
            {var subQ0=sQuery(id+"F0.wireOp",EDGE,"E18");var subQ1=sQuery(id+"F0.wireOp",EDGE,"E1");var subQ2=makeQuery(id+"F0.imprint","INTERSECT",VERTEX,{"disambiguationData":[OD(1.0)],"derivedFrom":[subQ1,subQ0]});Q68=makeQuery(id+"F0.imprint","IMPRINT",FACE,{"disambiguationData":[TD([[makeQuery(id+"F0.imprint","IMPRINT",EDGE,{"disambiguationData":[TD([[subQ2,-1.0]])],"derivedFrom":subQ1}),1.0]])]});}
            var Q69;
            {var subQ0=sQuery(id+"F0.wireOp",EDGE,"E18");var subQ1=sQuery(id+"F0.wireOp",EDGE,"E1");var subQ2=makeQuery(id+"F0.imprint","INTERSECT",VERTEX,{"disambiguationData":[OD(0.0)],"derivedFrom":[subQ1,subQ0]});Q69=makeQuery(id+"F0.imprint","IMPRINT",FACE,{"disambiguationData":[TD([[makeQuery(id+"F0.imprint","IMPRINT",EDGE,{"disambiguationData":[TD([[subQ2,-1.0]])],"derivedFrom":subQ1}),1.0]])]});}
            var Q70;
            {var subQ0=sQuery(id+"F0.wireOp",EDGE,"E16.right");var subQ1=sQuery(id+"F0.wireOp",EDGE,"E1");var subQ2=makeQuery(id+"F0.imprint","INTERSECT",VERTEX,{"derivedFrom":[subQ1,subQ0]});Q70=makeQuery(id+"F0.imprint","IMPRINT",FACE,{"disambiguationData":[TD([[makeQuery(id+"F0.imprint","IMPRINT",EDGE,{"disambiguationData":[TD([[subQ2,1.0]])],"derivedFrom":subQ0}),1.0]])]});}
            var Q71;
            {var subQ3=sQuery(id+"F0.wireOp",EDGE,"E7");var subQ7=sQuery(id+"F0.wireOp",EDGE,"E4");var subQ8=makeQuery(id+"F0.imprint","INTERSECT",VERTEX,{"disambiguationData":[OD(1.0)],"derivedFrom":[subQ7,subQ3]});Q71=makeQuery(id+"F0.imprint","IMPRINT",FACE,{"disambiguationData":[TD([[makeQuery(id+"F0.imprint","IMPRINT",EDGE,{"disambiguationData":[TD([[subQ8,-1.0]])],"derivedFrom":subQ7}),1.0]])]});}
            var Q72;
            {var subQ0=sQuery(id+"F0.wireOp",EDGE,"E17.left");var subQ7=sQuery(id+"F0.wireOp",EDGE,"E4");var subQ8=makeQuery(id+"F0.imprint","INTERSECT",VERTEX,{"derivedFrom":[subQ7,subQ0]});Q72=makeQuery(id+"F0.imprint","IMPRINT",FACE,{"disambiguationData":[TD([[makeQuery(id+"F0.imprint","IMPRINT",EDGE,{"disambiguationData":[TD([[subQ8,-1.0]])],"derivedFrom":subQ7}),1.0]])]});}
            var Q73;
            {var subQ0=sQuery(id+"F0.wireOp",EDGE,"E24");var subQ1=sQuery(id+"F0.wireOp",EDGE,"E1");var subQ2=makeQuery(id+"F0.imprint","INTERSECT",VERTEX,{"disambiguationData":[OD(0.0)],"derivedFrom":[subQ1,subQ0]});Q73=makeQuery(id+"F0.imprint","IMPRINT",FACE,{"disambiguationData":[TD([[makeQuery(id+"F0.imprint","IMPRINT",EDGE,{"disambiguationData":[TD([[subQ2,-1.0]])],"derivedFrom":subQ1}),1.0]])]});}
            var Q74;
            {var subQ0=sQuery(id+"F0.wireOp",EDGE,"E20.left");var subQ5=sQuery(id+"F0.wireOp",EDGE,"E20.bottom");var subQ7=makeQuery(id+"F0.imprint","INTERSECT",VERTEX,{"derivedFrom":[subQ5,subQ0]});Q74=makeQuery(id+"F0.imprint","IMPRINT",FACE,{"disambiguationData":[TD([[makeQuery(id+"F0.imprint","IMPRINT",EDGE,{"disambiguationData":[TD([[subQ7,-1.0]])],"derivedFrom":subQ5}),-1.0]])]});}
            var Q75;
            {var subQ0=sQuery(id+"F0.wireOp",EDGE,"E20.right");var subQ5=sQuery(id+"F0.wireOp",EDGE,"E20.bottom");var subQ7=makeQuery(id+"F0.imprint","INTERSECT",VERTEX,{"derivedFrom":[subQ5,subQ0]});Q75=makeQuery(id+"F0.imprint","IMPRINT",FACE,{"disambiguationData":[TD([[makeQuery(id+"F0.imprint","IMPRINT",EDGE,{"disambiguationData":[TD([[subQ7,1.0]])],"derivedFrom":subQ5}),-1.0]])]});}
            var Q76;
            {var subQ0=sQuery(id+"F0.wireOp",EDGE,"E16.right");var subQ3=sQuery(id+"F0.wireOp",EDGE,"E16.top");var subQ5=makeQuery(id+"F0.imprint","INTERSECT",VERTEX,{"derivedFrom":[subQ3,subQ0]});Q76=makeQuery(id+"F0.imprint","IMPRINT",FACE,{"disambiguationData":[TD([[makeQuery(id+"F0.imprint","IMPRINT",EDGE,{"disambiguationData":[TD([[subQ5,1.0]])],"derivedFrom":subQ0}),1.0]])]});}
            var Q77;
            {var subQ0=sQuery(id+"F0.wireOp",EDGE,"E16.left");var subQ3=sQuery(id+"F0.wireOp",EDGE,"E16.top");var subQ5=makeQuery(id+"F0.imprint","INTERSECT",VERTEX,{"derivedFrom":[subQ3,subQ0]});Q77=makeQuery(id+"F0.imprint","IMPRINT",FACE,{"disambiguationData":[TD([[makeQuery(id+"F0.imprint","IMPRINT",EDGE,{"disambiguationData":[TD([[subQ5,1.0]])],"derivedFrom":subQ0}),-1.0]])]});}
            var Q78;
            {var subQ0=sQuery(id+"F0.wireOp",EDGE,"E19.right");var subQ3=sQuery(id+"F0.wireOp",EDGE,"E19.top");var subQ5=makeQuery(id+"F0.imprint","INTERSECT",VERTEX,{"derivedFrom":[subQ3,subQ0]});Q78=makeQuery(id+"F0.imprint","IMPRINT",FACE,{"disambiguationData":[TD([[makeQuery(id+"F0.imprint","IMPRINT",EDGE,{"disambiguationData":[TD([[subQ5,1.0]])],"derivedFrom":subQ0}),-1.0]])]});}
            var Q79;
            {var subQ0=sQuery(id+"F0.wireOp",EDGE,"E19.left");var subQ3=sQuery(id+"F0.wireOp",EDGE,"E19.top");var subQ5=makeQuery(id+"F0.imprint","INTERSECT",VERTEX,{"derivedFrom":[subQ3,subQ0]});Q79=makeQuery(id+"F0.imprint","IMPRINT",FACE,{"disambiguationData":[TD([[makeQuery(id+"F0.imprint","IMPRINT",EDGE,{"disambiguationData":[TD([[subQ5,1.0]])],"derivedFrom":subQ0}),1.0]])]});}
            var Q80;
            {var subQ0=sQuery(id+"F0.wireOp",EDGE,"E17.left");var subQ1=sQuery(id+"F0.wireOp",EDGE,"E4");var subQ2=makeQuery(id+"F0.imprint","INTERSECT",VERTEX,{"derivedFrom":[subQ1,subQ0]});Q80=makeQuery(id+"F0.imprint","IMPRINT",FACE,{"disambiguationData":[TD([[makeQuery(id+"F0.imprint","IMPRINT",EDGE,{"disambiguationData":[TD([[subQ2,1.0]])],"derivedFrom":subQ1}),-1.0]])]});}
            var Q81;
            {var subQ0=sQuery(id+"F0.wireOp",EDGE,"E17.right");var subQ1=sQuery(id+"F0.wireOp",EDGE,"E4");var subQ2=makeQuery(id+"F0.imprint","INTERSECT",VERTEX,{"derivedFrom":[subQ1,subQ0]});Q81=makeQuery(id+"F0.imprint","IMPRINT",FACE,{"disambiguationData":[TD([[makeQuery(id+"F0.imprint","IMPRINT",EDGE,{"disambiguationData":[TD([[subQ2,-1.0]])],"derivedFrom":subQ1}),-1.0]])]});}
            var Q82;
            {var subQ0=sQuery(id+"F0.wireOp",EDGE,"E20.left");var subQ1=sQuery(id+"F0.wireOp",EDGE,"E4");var subQ2=makeQuery(id+"F0.imprint","INTERSECT",VERTEX,{"derivedFrom":[subQ1,subQ0]});Q82=makeQuery(id+"F0.imprint","IMPRINT",FACE,{"disambiguationData":[TD([[makeQuery(id+"F0.imprint","IMPRINT",EDGE,{"disambiguationData":[TD([[subQ2,-1.0]])],"derivedFrom":subQ1}),-1.0]])]});}
            var Q83;
            {var subQ0=sQuery(id+"F0.wireOp",EDGE,"E20.right");var subQ1=sQuery(id+"F0.wireOp",EDGE,"E4");var subQ2=makeQuery(id+"F0.imprint","INTERSECT",VERTEX,{"derivedFrom":[subQ1,subQ0]});Q83=makeQuery(id+"F0.imprint","IMPRINT",FACE,{"disambiguationData":[TD([[makeQuery(id+"F0.imprint","IMPRINT",EDGE,{"disambiguationData":[TD([[subQ2,1.0]])],"derivedFrom":subQ1}),-1.0]])]});}
            var Q84;
            {var subQ3=sQuery(id+"F0.wireOp",EDGE,"E4");var subQ7=sQuery(id+"F0.wireOp",EDGE,"E7");var subQ9=makeQuery(id+"F0.imprint","INTERSECT",VERTEX,{"disambiguationData":[OD(1.0)],"derivedFrom":[subQ3,subQ7]});Q84=makeQuery(id+"F0.imprint","IMPRINT",FACE,{"disambiguationData":[TD([[makeQuery(id+"F0.imprint","IMPRINT",EDGE,{"disambiguationData":[TD([[subQ9,-1.0]])],"derivedFrom":subQ3}),-1.0]])]});}
            var Q85;
            {var subQ5=sQuery(id+"F0.wireOp",EDGE,"E6.bottom");var subQ7=sQuery(id+"F0.wireOp",EDGE,"E4");var subQ8=makeQuery(id+"F0.imprint","INTERSECT",VERTEX,{"derivedFrom":[subQ7,subQ5]});Q85=makeQuery(id+"F0.imprint","IMPRINT",FACE,{"disambiguationData":[TD([[makeQuery(id+"F0.imprint","IMPRINT",EDGE,{"disambiguationData":[TD([[subQ8,-1.0]])],"derivedFrom":subQ7}),-1.0]])]});}
            var Q86;
            {var subQ3=sQuery(id+"F0.wireOp",EDGE,"E4");var subQ7=sQuery(id+"F0.wireOp",EDGE,"E18");var subQ8=makeQuery(id+"F0.imprint","INTERSECT",VERTEX,{"disambiguationData":[OD(0.0)],"derivedFrom":[subQ3,subQ7]});Q86=makeQuery(id+"F0.imprint","IMPRINT",FACE,{"disambiguationData":[TD([[makeQuery(id+"F0.imprint","IMPRINT",EDGE,{"disambiguationData":[TD([[subQ8,-1.0]])],"derivedFrom":subQ3}),-1.0]])]});}
            var Q87;
            {var subQ5=sQuery(id+"F0.wireOp",EDGE,"E20.right");var subQ7=sQuery(id+"F0.wireOp",EDGE,"E4");var subQ8=makeQuery(id+"F0.imprint","INTERSECT",VERTEX,{"derivedFrom":[subQ7,subQ5]});Q87=makeQuery(id+"F0.imprint","IMPRINT",FACE,{"disambiguationData":[TD([[makeQuery(id+"F0.imprint","IMPRINT",EDGE,{"disambiguationData":[TD([[subQ8,-1.0]])],"derivedFrom":subQ7}),-1.0]])]});}
            var Q88;
            {var subQ0=sQuery(id+"F0.wireOp",EDGE,"E21");var subQ1=sQuery(id+"F0.wireOp",EDGE,"E8");var subQ2=makeQuery(id+"F0.imprint","INTERSECT",VERTEX,{"disambiguationData":[OD(1.0)],"derivedFrom":[subQ1,subQ0]});Q88=makeQuery(id+"F0.imprint","IMPRINT",FACE,{"disambiguationData":[TD([[makeQuery(id+"F0.imprint","IMPRINT",EDGE,{"disambiguationData":[TD([[subQ2,1.0]])],"derivedFrom":subQ0}),1.0]])]});}
            var Q89;
            {var subQ3=sQuery(id+"F0.wireOp",EDGE,"E4");var subQ7=sQuery(id+"F0.wireOp",EDGE,"E7");var subQ8=makeQuery(id+"F0.imprint","INTERSECT",VERTEX,{"disambiguationData":[OD(0.0)],"derivedFrom":[subQ3,subQ7]});Q89=makeQuery(id+"F0.imprint","IMPRINT",FACE,{"disambiguationData":[TD([[makeQuery(id+"F0.imprint","IMPRINT",EDGE,{"disambiguationData":[TD([[subQ8,-1.0]])],"derivedFrom":subQ3}),-1.0]])]});}
            var Q90;
            {var subQ5=sQuery(id+"F0.wireOp",EDGE,"E15.MirrorCS");var subQ7=sQuery(id+"F0.wireOp",EDGE,"E4");var subQ8=makeQuery(id+"F0.imprint","INTERSECT",VERTEX,{"derivedFrom":[subQ7,subQ5]});Q90=makeQuery(id+"F0.imprint","IMPRINT",FACE,{"disambiguationData":[TD([[makeQuery(id+"F0.imprint","IMPRINT",EDGE,{"disambiguationData":[TD([[subQ8,-1.0]])],"derivedFrom":subQ7}),-1.0]])]});}
            var Q91;
            {var subQ5=sQuery(id+"F0.wireOp",EDGE,"E4");var subQ7=sQuery(id+"F0.wireOp",EDGE,"E18");var subQ8=makeQuery(id+"F0.imprint","INTERSECT",VERTEX,{"disambiguationData":[OD(1.0)],"derivedFrom":[subQ5,subQ7]});Q91=makeQuery(id+"F0.imprint","IMPRINT",FACE,{"disambiguationData":[TD([[makeQuery(id+"F0.imprint","IMPRINT",EDGE,{"disambiguationData":[TD([[subQ8,-1.0]])],"derivedFrom":subQ5}),-1.0]])]});}
            var Q92;
            {var subQ0=sQuery(id+"F0.wireOp",EDGE,"E21");var subQ1=sQuery(id+"F0.wireOp",EDGE,"E8");var subQ2=makeQuery(id+"F0.imprint","INTERSECT",VERTEX,{"disambiguationData":[OD(0.0)],"derivedFrom":[subQ1,subQ0]});Q92=makeQuery(id+"F0.imprint","IMPRINT",FACE,{"disambiguationData":[TD([[makeQuery(id+"F0.imprint","IMPRINT",EDGE,{"disambiguationData":[TD([[subQ2,-1.0]])],"derivedFrom":subQ0}),1.0]])]});}
            var Q93;
            {var subQ1=sQuery(id+"F0.wireOp",EDGE,"E11.MirrorCS");var subQ3=sQuery(id+"F0.wireOp",EDGE,"E21");var subQ4=makeQuery(id+"F0.imprint","INTERSECT",VERTEX,{"derivedFrom":[subQ1,subQ3]});Q93=makeQuery(id+"F0.imprint","IMPRINT",FACE,{"disambiguationData":[TD([[makeQuery(id+"F0.imprint","IMPRINT",EDGE,{"disambiguationData":[TD([[subQ4,-1.0]])],"derivedFrom":subQ3}),1.0]])]});}
            var Q94;
            {var subQ5=sQuery(id+"F0.wireOp",EDGE,"E17.left");var subQ7=sQuery(id+"F0.wireOp",EDGE,"E4");var subQ8=makeQuery(id+"F0.imprint","INTERSECT",VERTEX,{"derivedFrom":[subQ7,subQ5]});Q94=makeQuery(id+"F0.imprint","IMPRINT",FACE,{"disambiguationData":[TD([[makeQuery(id+"F0.imprint","IMPRINT",EDGE,{"disambiguationData":[TD([[subQ8,-1.0]])],"derivedFrom":subQ7}),-1.0]])]});}
            var Q95;
            {var subQ1=sQuery(id+"F0.wireOp",EDGE,"E5.bottom");var subQ3=sQuery(id+"F0.wireOp",EDGE,"E21");var subQ4=makeQuery(id+"F0.imprint","INTERSECT",VERTEX,{"derivedFrom":[subQ1,subQ3]});Q95=makeQuery(id+"F0.imprint","IMPRINT",FACE,{"disambiguationData":[TD([[makeQuery(id+"F0.imprint","IMPRINT",EDGE,{"disambiguationData":[TD([[subQ4,-1.0]])],"derivedFrom":subQ3}),1.0]])]});}
            var Q96;
            {var subQ0=sQuery(id+"F0.wireOp",EDGE,"E16.left");var subQ1=sQuery(id+"F0.wireOp",EDGE,"E1");var subQ2=makeQuery(id+"F0.imprint","INTERSECT",VERTEX,{"derivedFrom":[subQ1,subQ0]});Q96=makeQuery(id+"F0.imprint","IMPRINT",FACE,{"disambiguationData":[TD([[makeQuery(id+"F0.imprint","IMPRINT",EDGE,{"disambiguationData":[TD([[subQ2,1.0]])],"derivedFrom":subQ0}),-1.0]])]});}
            var Q97;
            {var subQ0=sQuery(id+"F0.wireOp",EDGE,"E21");var subQ1=sQuery(id+"F0.wireOp",EDGE,"E8");var subQ2=makeQuery(id+"F0.imprint","INTERSECT",VERTEX,{"disambiguationData":[OD(0.0)],"derivedFrom":[subQ1,subQ0]});Q97=makeQuery(id+"F0.imprint","IMPRINT",FACE,{"disambiguationData":[TD([[makeQuery(id+"F0.imprint","IMPRINT",EDGE,{"disambiguationData":[TD([[subQ2,1.0]])],"derivedFrom":subQ0}),1.0]])]});}
            var Q98;
            {var subQ0=sQuery(id+"F0.wireOp",EDGE,"E5.top");var subQ1=sQuery(id+"F0.wireOp",EDGE,"E1");var subQ2=makeQuery(id+"F0.imprint","INTERSECT",VERTEX,{"derivedFrom":[subQ1,subQ0]});Q98=makeQuery(id+"F0.imprint","IMPRINT",FACE,{"disambiguationData":[TD([[makeQuery(id+"F0.imprint","IMPRINT",EDGE,{"disambiguationData":[TD([[subQ2,1.0]])],"derivedFrom":subQ0}),-1.0]])]});}
            var Q99;
            {var subQ1=sQuery(id+"F0.wireOp",EDGE,"E5.top");var subQ3=sQuery(id+"F0.wireOp",EDGE,"E21");var subQ4=makeQuery(id+"F0.imprint","INTERSECT",VERTEX,{"derivedFrom":[subQ1,subQ3]});Q99=makeQuery(id+"F0.imprint","IMPRINT",FACE,{"disambiguationData":[TD([[makeQuery(id+"F0.imprint","IMPRINT",EDGE,{"disambiguationData":[TD([[subQ4,1.0]])],"derivedFrom":subQ3}),1.0]])]});}
            var Q100;
            {var subQ1=sQuery(id+"F0.wireOp",EDGE,"E13.MirrorCS");var subQ3=sQuery(id+"F0.wireOp",EDGE,"E21");var subQ4=makeQuery(id+"F0.imprint","INTERSECT",VERTEX,{"derivedFrom":[subQ1,subQ3]});Q100=makeQuery(id+"F0.imprint","IMPRINT",FACE,{"disambiguationData":[TD([[makeQuery(id+"F0.imprint","IMPRINT",EDGE,{"disambiguationData":[TD([[subQ4,1.0]])],"derivedFrom":subQ3}),1.0]])]});}
            var Q101;
            {var subQ0=sQuery(id+"F0.wireOp",EDGE,"E11.MirrorCS");var subQ1=sQuery(id+"F0.wireOp",EDGE,"E1");var subQ2=makeQuery(id+"F0.imprint","INTERSECT",VERTEX,{"derivedFrom":[subQ1,subQ0]});Q101=makeQuery(id+"F0.imprint","IMPRINT",FACE,{"disambiguationData":[TD([[makeQuery(id+"F0.imprint","IMPRINT",EDGE,{"disambiguationData":[TD([[subQ2,1.0]])],"derivedFrom":subQ0}),1.0]])]});}
            var Q102;
            {var subQ0=sQuery(id+"F0.wireOp",EDGE,"E19.right");var subQ1=sQuery(id+"F0.wireOp",EDGE,"E1");var subQ2=makeQuery(id+"F0.imprint","INTERSECT",VERTEX,{"derivedFrom":[subQ1,subQ0]});Q102=makeQuery(id+"F0.imprint","IMPRINT",FACE,{"disambiguationData":[TD([[makeQuery(id+"F0.imprint","IMPRINT",EDGE,{"disambiguationData":[TD([[subQ2,1.0]])],"derivedFrom":subQ0}),-1.0]])]});}
            var Q103;
            {var subQ0=sQuery(id+"F0.wireOp",EDGE,"E21");var subQ1=sQuery(id+"F0.wireOp",EDGE,"E8");var subQ2=makeQuery(id+"F0.imprint","INTERSECT",VERTEX,{"disambiguationData":[OD(1.0)],"derivedFrom":[subQ1,subQ0]});Q103=makeQuery(id+"F0.imprint","IMPRINT",FACE,{"disambiguationData":[TD([[makeQuery(id+"F0.imprint","IMPRINT",EDGE,{"disambiguationData":[TD([[subQ2,-1.0]])],"derivedFrom":subQ0}),1.0]])]});}
            var Q104;
            {var subQ0=sQuery(id+"F0.wireOp",EDGE,"E25");var subQ1=sQuery(id+"F0.wireOp",EDGE,"E4");var subQ2=makeQuery(id+"F0.imprint","INTERSECT",VERTEX,{"disambiguationData":[OD(0.0)],"derivedFrom":[subQ1,subQ0]});Q104=makeQuery(id+"F0.imprint","IMPRINT",FACE,{"disambiguationData":[TD([[makeQuery(id+"F0.imprint","IMPRINT",EDGE,{"disambiguationData":[TD([[subQ2,-1.0]])],"derivedFrom":subQ1}),1.0]])]});}
            var Q105;
            {var subQ0=sQuery(id+"F0.wireOp",EDGE,"E5.top");var subQ1=sQuery(id+"F0.wireOp",EDGE,"E1");var subQ2=makeQuery(id+"F0.imprint","INTERSECT",VERTEX,{"derivedFrom":[subQ1,subQ0]});Q105=makeQuery(id+"F0.imprint","IMPRINT",FACE,{"disambiguationData":[TD([[makeQuery(id+"F0.imprint","IMPRINT",EDGE,{"disambiguationData":[TD([[subQ2,-1.0]])],"derivedFrom":subQ1}),1.0]])]});}
            var Q106;
            {var subQ0=sQuery(id+"F0.wireOp",EDGE,"E26");var subQ1=sQuery(id+"F0.wireOp",EDGE,"E1");var subQ2=makeQuery(id+"F0.imprint","INTERSECT",VERTEX,{"disambiguationData":[OD(0.0)],"derivedFrom":[subQ1,subQ0]});Q106=makeQuery(id+"F0.imprint","IMPRINT",FACE,{"disambiguationData":[TD([[makeQuery(id+"F0.imprint","IMPRINT",EDGE,{"disambiguationData":[TD([[subQ2,-1.0]])],"derivedFrom":subQ1}),1.0]])]});}
            var Q107;
            {var subQ0=sQuery(id+"F0.wireOp",EDGE,"E26");var subQ1=sQuery(id+"F0.wireOp",EDGE,"E1");var subQ2=makeQuery(id+"F0.imprint","INTERSECT",VERTEX,{"disambiguationData":[OD(1.0)],"derivedFrom":[subQ1,subQ0]});Q107=makeQuery(id+"F0.imprint","IMPRINT",FACE,{"disambiguationData":[TD([[makeQuery(id+"F0.imprint","IMPRINT",EDGE,{"disambiguationData":[TD([[subQ2,-1.0]])],"derivedFrom":subQ1}),1.0]])]});}
            var Q108;
            {var subQ0=sQuery(id+"F0.wireOp",EDGE,"E16.left");var subQ1=sQuery(id+"F0.wireOp",EDGE,"E1");var subQ2=makeQuery(id+"F0.imprint","INTERSECT",VERTEX,{"derivedFrom":[subQ1,subQ0]});Q108=makeQuery(id+"F0.imprint","IMPRINT",FACE,{"disambiguationData":[TD([[makeQuery(id+"F0.imprint","IMPRINT",EDGE,{"disambiguationData":[TD([[subQ2,-1.0]])],"derivedFrom":subQ1}),1.0]])]});}
            var Q109;
            {var subQ0=sQuery(id+"F0.wireOp",EDGE,"E24");var subQ1=sQuery(id+"F0.wireOp",EDGE,"E4");var subQ2=makeQuery(id+"F0.imprint","INTERSECT",VERTEX,{"disambiguationData":[OD(0.0)],"derivedFrom":[subQ1,subQ0]});Q109=makeQuery(id+"F0.imprint","IMPRINT",FACE,{"disambiguationData":[TD([[makeQuery(id+"F0.imprint","IMPRINT",EDGE,{"disambiguationData":[TD([[subQ2,-1.0]])],"derivedFrom":subQ1}),1.0]])]});}
            var Q110;
            {var subQ0=sQuery(id+"F0.wireOp",EDGE,"E24");var subQ1=sQuery(id+"F0.wireOp",EDGE,"E4");var subQ2=makeQuery(id+"F0.imprint","INTERSECT",VERTEX,{"disambiguationData":[OD(0.0)],"derivedFrom":[subQ1,subQ0]});Q110=makeQuery(id+"F0.imprint","IMPRINT",FACE,{"disambiguationData":[TD([[makeQuery(id+"F0.imprint","IMPRINT",EDGE,{"disambiguationData":[TD([[subQ2,-1.0]])],"derivedFrom":subQ1}),-1.0]])]});}
            var Q111;
            {var subQ0=sQuery(id+"F0.wireOp",EDGE,"E27");var subQ1=sQuery(id+"F0.wireOp",EDGE,"E4");var subQ2=makeQuery(id+"F0.imprint","INTERSECT",VERTEX,{"disambiguationData":[OD(0.0)],"derivedFrom":[subQ1,subQ0]});Q111=makeQuery(id+"F0.imprint","IMPRINT",FACE,{"disambiguationData":[TD([[makeQuery(id+"F0.imprint","IMPRINT",EDGE,{"disambiguationData":[TD([[subQ2,-1.0]])],"derivedFrom":subQ1}),1.0]])]});}
            var Q112;
            {var subQ0=sQuery(id+"F0.wireOp",EDGE,"E25");var subQ1=sQuery(id+"F0.wireOp",EDGE,"E1");var subQ2=makeQuery(id+"F0.imprint","INTERSECT",VERTEX,{"disambiguationData":[OD(0.0)],"derivedFrom":[subQ1,subQ0]});Q112=makeQuery(id+"F0.imprint","IMPRINT",FACE,{"disambiguationData":[TD([[makeQuery(id+"F0.imprint","IMPRINT",EDGE,{"disambiguationData":[TD([[subQ2,-1.0]])],"derivedFrom":subQ1}),1.0]])]});}
            var Q113;
            {var subQ0=sQuery(id+"F0.wireOp",EDGE,"E7");var subQ1=sQuery(id+"F0.wireOp",EDGE,"E1");var subQ2=makeQuery(id+"F0.imprint","INTERSECT",VERTEX,{"disambiguationData":[OD(1.0)],"derivedFrom":[subQ1,subQ0]});Q113=makeQuery(id+"F0.imprint","IMPRINT",FACE,{"disambiguationData":[TD([[makeQuery(id+"F0.imprint","IMPRINT",EDGE,{"disambiguationData":[TD([[subQ2,-1.0]])],"derivedFrom":subQ1}),-1.0]])]});}
            var Q114;
            {var subQ0=sQuery(id+"F0.wireOp",EDGE,"E27");var subQ1=sQuery(id+"F0.wireOp",EDGE,"E4");var subQ2=makeQuery(id+"F0.imprint","INTERSECT",VERTEX,{"disambiguationData":[OD(1.0)],"derivedFrom":[subQ1,subQ0]});Q114=makeQuery(id+"F0.imprint","IMPRINT",FACE,{"disambiguationData":[TD([[makeQuery(id+"F0.imprint","IMPRINT",EDGE,{"disambiguationData":[TD([[subQ2,-1.0]])],"derivedFrom":subQ1}),-1.0]])]});}
            var Q115;
            {var subQ0=sQuery(id+"F0.wireOp",EDGE,"E26");var subQ1=sQuery(id+"F0.wireOp",EDGE,"E4");var subQ2=makeQuery(id+"F0.imprint","INTERSECT",VERTEX,{"disambiguationData":[OD(0.0)],"derivedFrom":[subQ1,subQ0]});Q115=makeQuery(id+"F0.imprint","IMPRINT",FACE,{"disambiguationData":[TD([[makeQuery(id+"F0.imprint","IMPRINT",EDGE,{"disambiguationData":[TD([[subQ2,-1.0]])],"derivedFrom":subQ1}),1.0]])]});}
            var Q116;
            {var subQ4=sQuery(id+"F0.wireOp",EDGE,"E1");var subQ8=sQuery(id+"F0.wireOp",EDGE,"E19.right");var subQ10=makeQuery(id+"F0.imprint","INTERSECT",VERTEX,{"derivedFrom":[subQ4,subQ8]});Q116=makeQuery(id+"F0.imprint","IMPRINT",FACE,{"disambiguationData":[TD([[makeQuery(id+"F0.imprint","IMPRINT",EDGE,{"disambiguationData":[TD([[subQ10,-1.0]])],"derivedFrom":subQ4}),-1.0]])]});}
            var Q117;
            {var subQ1=sQuery(id+"F0.wireOp",EDGE,"E5.top");var subQ3=sQuery(id+"F0.wireOp",EDGE,"E1");var subQ4=makeQuery(id+"F0.imprint","INTERSECT",VERTEX,{"derivedFrom":[subQ3,subQ1]});Q117=makeQuery(id+"F0.imprint","IMPRINT",FACE,{"disambiguationData":[TD([[makeQuery(id+"F0.imprint","IMPRINT",EDGE,{"disambiguationData":[TD([[subQ4,-1.0]])],"derivedFrom":subQ3}),-1.0]])]});}
            var Q118;
            {var subQ0=sQuery(id+"F0.wireOp",EDGE,"E25");var subQ1=sQuery(id+"F0.wireOp",EDGE,"E4");var subQ2=makeQuery(id+"F0.imprint","INTERSECT",VERTEX,{"disambiguationData":[OD(1.0)],"derivedFrom":[subQ1,subQ0]});Q118=makeQuery(id+"F0.imprint","IMPRINT",FACE,{"disambiguationData":[TD([[makeQuery(id+"F0.imprint","IMPRINT",EDGE,{"disambiguationData":[TD([[subQ2,-1.0]])],"derivedFrom":subQ1}),1.0]])]});}
            var Q119;
            {var subQ4=sQuery(id+"F0.wireOp",EDGE,"E1");var subQ9=sQuery(id+"F0.wireOp",EDGE,"E18");var subQ11=makeQuery(id+"F0.imprint","INTERSECT",VERTEX,{"disambiguationData":[OD(1.0)],"derivedFrom":[subQ4,subQ9]});Q119=makeQuery(id+"F0.imprint","IMPRINT",FACE,{"disambiguationData":[TD([[makeQuery(id+"F0.imprint","IMPRINT",EDGE,{"disambiguationData":[TD([[subQ11,-1.0]])],"derivedFrom":subQ4}),-1.0]])]});}
            var Q120;
            {var subQ0=sQuery(id+"F0.wireOp",EDGE,"E26");var subQ1=sQuery(id+"F0.wireOp",EDGE,"E4");var subQ2=makeQuery(id+"F0.imprint","INTERSECT",VERTEX,{"disambiguationData":[OD(1.0)],"derivedFrom":[subQ1,subQ0]});Q120=makeQuery(id+"F0.imprint","IMPRINT",FACE,{"disambiguationData":[TD([[makeQuery(id+"F0.imprint","IMPRINT",EDGE,{"disambiguationData":[TD([[subQ2,-1.0]])],"derivedFrom":subQ1}),-1.0]])]});}
            var Q121;
            {var subQ0=sQuery(id+"F0.wireOp",EDGE,"E7");var subQ1=sQuery(id+"F0.wireOp",EDGE,"E1");var subQ2=makeQuery(id+"F0.imprint","INTERSECT",VERTEX,{"disambiguationData":[OD(0.0)],"derivedFrom":[subQ1,subQ0]});Q121=makeQuery(id+"F0.imprint","IMPRINT",FACE,{"disambiguationData":[TD([[makeQuery(id+"F0.imprint","IMPRINT",EDGE,{"disambiguationData":[TD([[subQ2,-1.0]])],"derivedFrom":subQ1}),-1.0]])]});}
            var Q122;
            {var subQ0=sQuery(id+"F0.wireOp",EDGE,"E25");var subQ1=sQuery(id+"F0.wireOp",EDGE,"E4");var subQ2=makeQuery(id+"F0.imprint","INTERSECT",VERTEX,{"disambiguationData":[OD(0.0)],"derivedFrom":[subQ1,subQ0]});Q122=makeQuery(id+"F0.imprint","IMPRINT",FACE,{"disambiguationData":[TD([[makeQuery(id+"F0.imprint","IMPRINT",EDGE,{"disambiguationData":[TD([[subQ2,-1.0]])],"derivedFrom":subQ1}),-1.0]])]});}
            var Q123;
            {var subQ0=sQuery(id+"F0.wireOp",EDGE,"E19.right");var subQ1=sQuery(id+"F0.wireOp",EDGE,"E1");var subQ2=makeQuery(id+"F0.imprint","INTERSECT",VERTEX,{"derivedFrom":[subQ1,subQ0]});Q123=makeQuery(id+"F0.imprint","IMPRINT",FACE,{"disambiguationData":[TD([[makeQuery(id+"F0.imprint","IMPRINT",EDGE,{"disambiguationData":[TD([[subQ2,-1.0]])],"derivedFrom":subQ1}),1.0]])]});}
            var Q124;
            {var subQ0=sQuery(id+"F0.wireOp",EDGE,"E27");var subQ1=sQuery(id+"F0.wireOp",EDGE,"E4");var subQ2=makeQuery(id+"F0.imprint","INTERSECT",VERTEX,{"disambiguationData":[OD(0.0)],"derivedFrom":[subQ1,subQ0]});Q124=makeQuery(id+"F0.imprint","IMPRINT",FACE,{"disambiguationData":[TD([[makeQuery(id+"F0.imprint","IMPRINT",EDGE,{"disambiguationData":[TD([[subQ2,-1.0]])],"derivedFrom":subQ1}),-1.0]])]});}
            var Q125;
            {var subQ0=sQuery(id+"F0.wireOp",EDGE,"E24");var subQ1=sQuery(id+"F0.wireOp",EDGE,"E4");var subQ2=makeQuery(id+"F0.imprint","INTERSECT",VERTEX,{"disambiguationData":[OD(1.0)],"derivedFrom":[subQ1,subQ0]});Q125=makeQuery(id+"F0.imprint","IMPRINT",FACE,{"disambiguationData":[TD([[makeQuery(id+"F0.imprint","IMPRINT",EDGE,{"disambiguationData":[TD([[subQ2,-1.0]])],"derivedFrom":subQ1}),-1.0]])]});}
            var Q126;
            {var subQ0=sQuery(id+"F0.wireOp",EDGE,"E16.left");var subQ4=sQuery(id+"F0.wireOp",EDGE,"E1");var subQ11=makeQuery(id+"F0.imprint","INTERSECT",VERTEX,{"derivedFrom":[subQ4,subQ0]});Q126=makeQuery(id+"F0.imprint","IMPRINT",FACE,{"disambiguationData":[TD([[makeQuery(id+"F0.imprint","IMPRINT",EDGE,{"disambiguationData":[TD([[subQ11,-1.0]])],"derivedFrom":subQ4}),-1.0]])]});}
            var Q127;
            {var subQ0=sQuery(id+"F0.wireOp",EDGE,"E25");var subQ1=sQuery(id+"F0.wireOp",EDGE,"E1");var subQ2=makeQuery(id+"F0.imprint","INTERSECT",VERTEX,{"disambiguationData":[OD(1.0)],"derivedFrom":[subQ1,subQ0]});Q127=makeQuery(id+"F0.imprint","IMPRINT",FACE,{"disambiguationData":[TD([[makeQuery(id+"F0.imprint","IMPRINT",EDGE,{"disambiguationData":[TD([[subQ2,-1.0]])],"derivedFrom":subQ1}),1.0]])]});}
            var Q128;
            {var subQ3=sQuery(id+"F0.wireOp",EDGE,"E1");var subQ7=sQuery(id+"F0.wireOp",EDGE,"E18");var subQ11=makeQuery(id+"F0.imprint","INTERSECT",VERTEX,{"disambiguationData":[OD(0.0)],"derivedFrom":[subQ3,subQ7]});Q128=makeQuery(id+"F0.imprint","IMPRINT",FACE,{"disambiguationData":[TD([[makeQuery(id+"F0.imprint","IMPRINT",EDGE,{"disambiguationData":[TD([[subQ11,-1.0]])],"derivedFrom":subQ3}),-1.0]])]});}
            var Q129;
            {var subQ0=sQuery(id+"F0.wireOp",EDGE,"E26");var subQ1=sQuery(id+"F0.wireOp",EDGE,"E4");var subQ2=makeQuery(id+"F0.imprint","INTERSECT",VERTEX,{"disambiguationData":[OD(0.0)],"derivedFrom":[subQ1,subQ0]});Q129=makeQuery(id+"F0.imprint","IMPRINT",FACE,{"disambiguationData":[TD([[makeQuery(id+"F0.imprint","IMPRINT",EDGE,{"disambiguationData":[TD([[subQ2,-1.0]])],"derivedFrom":subQ1}),-1.0]])]});}
            var Q130;
            {var subQ0=sQuery(id+"F0.wireOp",EDGE,"E25");var subQ1=sQuery(id+"F0.wireOp",EDGE,"E4");var subQ2=makeQuery(id+"F0.imprint","INTERSECT",VERTEX,{"disambiguationData":[OD(1.0)],"derivedFrom":[subQ1,subQ0]});Q130=makeQuery(id+"F0.imprint","IMPRINT",FACE,{"disambiguationData":[TD([[makeQuery(id+"F0.imprint","IMPRINT",EDGE,{"disambiguationData":[TD([[subQ2,-1.0]])],"derivedFrom":subQ1}),-1.0]])]});}
            var Q131;
            {var subQ0=sQuery(id+"F0.wireOp",EDGE,"E13.MirrorCS");var subQ1=sQuery(id+"F0.wireOp",EDGE,"E1");var subQ2=makeQuery(id+"F0.imprint","INTERSECT",VERTEX,{"derivedFrom":[subQ1,subQ0]});Q131=makeQuery(id+"F0.imprint","IMPRINT",FACE,{"disambiguationData":[TD([[makeQuery(id+"F0.imprint","IMPRINT",EDGE,{"disambiguationData":[TD([[subQ2,-1.0]])],"derivedFrom":subQ1}),1.0]])]});}
            var Q132;
            {var subQ0=sQuery(id+"F0.wireOp",EDGE,"E24");var subQ1=sQuery(id+"F0.wireOp",EDGE,"E4");var subQ2=makeQuery(id+"F0.imprint","INTERSECT",VERTEX,{"disambiguationData":[OD(1.0)],"derivedFrom":[subQ1,subQ0]});Q132=makeQuery(id+"F0.imprint","IMPRINT",FACE,{"disambiguationData":[TD([[makeQuery(id+"F0.imprint","IMPRINT",EDGE,{"disambiguationData":[TD([[subQ2,-1.0]])],"derivedFrom":subQ1}),1.0]])]});}
            var Q133;
            {var subQ0=sQuery(id+"F0.wireOp",EDGE,"E26");var subQ1=sQuery(id+"F0.wireOp",EDGE,"E4");var subQ2=makeQuery(id+"F0.imprint","INTERSECT",VERTEX,{"disambiguationData":[OD(1.0)],"derivedFrom":[subQ1,subQ0]});Q133=makeQuery(id+"F0.imprint","IMPRINT",FACE,{"disambiguationData":[TD([[makeQuery(id+"F0.imprint","IMPRINT",EDGE,{"disambiguationData":[TD([[subQ2,-1.0]])],"derivedFrom":subQ1}),1.0]])]});}
            var Q134;
            {var subQ0=sQuery(id+"F0.wireOp",EDGE,"E27");var subQ1=sQuery(id+"F0.wireOp",EDGE,"E4");var subQ2=makeQuery(id+"F0.imprint","INTERSECT",VERTEX,{"disambiguationData":[OD(1.0)],"derivedFrom":[subQ1,subQ0]});Q134=makeQuery(id+"F0.imprint","IMPRINT",FACE,{"disambiguationData":[TD([[makeQuery(id+"F0.imprint","IMPRINT",EDGE,{"disambiguationData":[TD([[subQ2,-1.0]])],"derivedFrom":subQ1}),1.0]])]});}
            var Q135;
            {var subQ0=sQuery(id+"F0.wireOp",EDGE,"E13.MirrorCS");var subQ3=sQuery(id+"F0.wireOp",EDGE,"E1");var subQ4=makeQuery(id+"F0.imprint","INTERSECT",VERTEX,{"derivedFrom":[subQ3,subQ0]});Q135=makeQuery(id+"F0.imprint","IMPRINT",FACE,{"disambiguationData":[TD([[makeQuery(id+"F0.imprint","IMPRINT",EDGE,{"disambiguationData":[TD([[subQ4,-1.0]])],"derivedFrom":subQ3}),-1.0]])]});}
            var Q136;
            Q136=sQuery(id+"F0.wireOp",EDGE,"E1");
            var Q137;
            Q137=sQuery(id+"F0.wireOp",EDGE,"E3");
            var Q138;
            Q138=sQuery(id+"F0.wireOp",EDGE,"E2");
            var Q139;
            Q139=sQuery(id+"F0.wireOp",EDGE,"E0");
            extrude(context, id + "F1", {"entities" : qUnion([Q0, Q1, Q2, Q3, Q4, Q5, Q6, Q7, Q8, Q9, Q10, Q11, Q12, Q13, Q14, Q15, Q16, Q17, Q18, Q19, Q20, Q21, Q22, Q23, Q24, Q25, Q26, Q27, Q28, Q29, Q30, Q31, Q32, Q33, Q34, Q35, Q36, Q37, Q38, Q39, Q40, Q41, Q42, Q43, Q44, Q45, Q46, Q47, Q48, Q49, Q50, Q51, Q52, Q53, Q54, Q55, Q56, Q57, Q58, Q59, Q60, Q61, Q62, Q63, Q64, Q65, Q66, Q67, Q68, Q69, Q70, Q71, Q72, Q73, Q74, Q75, Q76, Q77, Q78, Q79, Q80, Q81, Q82, Q83, Q84, Q85, Q86, Q87, Q88, Q89, Q90, Q91, Q92, Q93, Q94, Q95, Q96, Q97, Q98, Q99, Q100, Q101, Q102, Q103, Q104, Q105, Q106, Q107, Q108, Q109, Q110, Q111, Q112, Q113, Q114, Q115, Q116, Q117, Q118, Q119, Q120, Q121, Q122, Q123, Q124, Q125, Q126, Q127, Q128, Q129, Q130, Q131, Q132, Q133, Q134, Q135]), "surfaceOperationType" : NewSurfaceOperationType.ADD, "surfaceEntities" : qUnion([Q136, Q137, Q138, Q139]), "depth" : 3 * mm, "offsetDistance" : 25 * mm});
        }
        {
            var Q0;
            Q0=makeQuery(id+"F0.imprint","IMPRINT",FACE,{"disambiguationData":[TD([[makeQuery(id+"F0.imprint","IMPRINT",EDGE,{"derivedFrom":sQuery(id+"F0.wireOp",EDGE,"E0")}),1.0]])]});
            var Q1;
            {var subQ5=sQuery(id+"F0.wireOp",EDGE,"E1");var subQ7=sQuery(id+"F0.wireOp",EDGE,"E7");var subQ8=makeQuery(id+"F0.imprint","INTERSECT",VERTEX,{"disambiguationData":[OD(0.0)],"derivedFrom":[subQ5,subQ7]});Q1=makeQuery(id+"F0.imprint","IMPRINT",FACE,{"disambiguationData":[TD([[makeQuery(id+"F0.imprint","IMPRINT",EDGE,{"disambiguationData":[TD([[subQ8,1.0]])],"derivedFrom":subQ5}),1.0]])]});}
            var Q2;
            {var subQ5=sQuery(id+"F0.wireOp",EDGE,"E7");var subQ6=sQuery(id+"F0.wireOp",EDGE,"E1");var subQ7=makeQuery(id+"F0.imprint","INTERSECT",VERTEX,{"disambiguationData":[OD(0.0)],"derivedFrom":[subQ6,subQ5]});Q2=makeQuery(id+"F0.imprint","IMPRINT",FACE,{"disambiguationData":[TD([[makeQuery(id+"F0.imprint","IMPRINT",EDGE,{"disambiguationData":[TD([[subQ7,-1.0]])],"derivedFrom":subQ6}),1.0]])]});}
            var Q3;
            {var subQ5=sQuery(id+"F0.wireOp",EDGE,"E1");var subQ7=sQuery(id+"F0.wireOp",EDGE,"E7");var subQ9=makeQuery(id+"F0.imprint","INTERSECT",VERTEX,{"disambiguationData":[OD(1.0)],"derivedFrom":[subQ5,subQ7]});Q3=makeQuery(id+"F0.imprint","IMPRINT",FACE,{"disambiguationData":[TD([[makeQuery(id+"F0.imprint","IMPRINT",EDGE,{"disambiguationData":[TD([[subQ9,-1.0]])],"derivedFrom":subQ5}),1.0]])]});}
            var Q4;
            {var subQ0=sQuery(id+"F0.wireOp",EDGE,"E7");var subQ1=sQuery(id+"F0.wireOp",EDGE,"E1");var subQ2=makeQuery(id+"F0.imprint","INTERSECT",VERTEX,{"disambiguationData":[OD(1.0)],"derivedFrom":[subQ1,subQ0]});Q4=makeQuery(id+"F0.imprint","IMPRINT",FACE,{"disambiguationData":[TD([[makeQuery(id+"F0.imprint","IMPRINT",EDGE,{"disambiguationData":[TD([[subQ2,1.0]])],"derivedFrom":subQ1}),1.0]])]});}
            var Q5;
            {var subQ5=sQuery(id+"F0.wireOp",EDGE,"E1");var subQ7=sQuery(id+"F0.wireOp",EDGE,"E18");var subQ8=makeQuery(id+"F0.imprint","INTERSECT",VERTEX,{"disambiguationData":[OD(0.0)],"derivedFrom":[subQ5,subQ7]});Q5=makeQuery(id+"F0.imprint","IMPRINT",FACE,{"disambiguationData":[TD([[makeQuery(id+"F0.imprint","IMPRINT",EDGE,{"disambiguationData":[TD([[subQ8,1.0]])],"derivedFrom":subQ5}),1.0]])]});}
            var Q6;
            {var subQ5=sQuery(id+"F0.wireOp",EDGE,"E18");var subQ7=sQuery(id+"F0.wireOp",EDGE,"E1");var subQ9=makeQuery(id+"F0.imprint","INTERSECT",VERTEX,{"disambiguationData":[OD(0.0)],"derivedFrom":[subQ7,subQ5]});Q6=makeQuery(id+"F0.imprint","IMPRINT",FACE,{"disambiguationData":[TD([[makeQuery(id+"F0.imprint","IMPRINT",EDGE,{"disambiguationData":[TD([[subQ9,-1.0]])],"derivedFrom":subQ7}),1.0]])]});}
            var Q7;
            {var subQ3=sQuery(id+"F0.wireOp",EDGE,"E18");var subQ7=sQuery(id+"F0.wireOp",EDGE,"E1");var subQ9=makeQuery(id+"F0.imprint","INTERSECT",VERTEX,{"disambiguationData":[OD(1.0)],"derivedFrom":[subQ7,subQ3]});Q7=makeQuery(id+"F0.imprint","IMPRINT",FACE,{"disambiguationData":[TD([[makeQuery(id+"F0.imprint","IMPRINT",EDGE,{"disambiguationData":[TD([[subQ9,1.0]])],"derivedFrom":subQ7}),1.0]])]});}
            var Q8;
            {var subQ5=sQuery(id+"F0.wireOp",EDGE,"E1");var subQ7=sQuery(id+"F0.wireOp",EDGE,"E18");var subQ9=makeQuery(id+"F0.imprint","INTERSECT",VERTEX,{"disambiguationData":[OD(1.0)],"derivedFrom":[subQ5,subQ7]});Q8=makeQuery(id+"F0.imprint","IMPRINT",FACE,{"disambiguationData":[TD([[makeQuery(id+"F0.imprint","IMPRINT",EDGE,{"disambiguationData":[TD([[subQ9,-1.0]])],"derivedFrom":subQ5}),1.0]])]});}
            var Q9;
            {var subQ3=sQuery(id+"F0.wireOp",EDGE,"E4");var subQ7=sQuery(id+"F0.wireOp",EDGE,"E7");var subQ8=makeQuery(id+"F0.imprint","INTERSECT",VERTEX,{"disambiguationData":[OD(1.0)],"derivedFrom":[subQ3,subQ7]});Q9=makeQuery(id+"F0.imprint","IMPRINT",FACE,{"disambiguationData":[TD([[makeQuery(id+"F0.imprint","IMPRINT",EDGE,{"disambiguationData":[TD([[subQ8,-1.0]])],"derivedFrom":subQ3}),-1.0]])]});}
            var Q10;
            {var subQ5=sQuery(id+"F0.wireOp",EDGE,"E18");var subQ6=sQuery(id+"F0.wireOp",EDGE,"E4");var subQ7=makeQuery(id+"F0.imprint","INTERSECT",VERTEX,{"disambiguationData":[OD(1.0)],"derivedFrom":[subQ6,subQ5]});Q10=makeQuery(id+"F0.imprint","IMPRINT",FACE,{"disambiguationData":[TD([[makeQuery(id+"F0.imprint","IMPRINT",EDGE,{"disambiguationData":[TD([[subQ7,-1.0]])],"derivedFrom":subQ6}),-1.0]])]});}
            var Q11;
            {var subQ0=sQuery(id+"F0.wireOp",EDGE,"E18");var subQ1=sQuery(id+"F0.wireOp",EDGE,"E4");var subQ2=makeQuery(id+"F0.imprint","INTERSECT",VERTEX,{"disambiguationData":[OD(0.0)],"derivedFrom":[subQ1,subQ0]});Q11=makeQuery(id+"F0.imprint","IMPRINT",FACE,{"disambiguationData":[TD([[makeQuery(id+"F0.imprint","IMPRINT",EDGE,{"disambiguationData":[TD([[subQ2,-1.0]])],"derivedFrom":subQ1}),-1.0]])]});}
            var Q12;
            {var subQ3=sQuery(id+"F0.wireOp",EDGE,"E4");var subQ7=sQuery(id+"F0.wireOp",EDGE,"E7");var subQ8=makeQuery(id+"F0.imprint","INTERSECT",VERTEX,{"disambiguationData":[OD(0.0)],"derivedFrom":[subQ3,subQ7]});Q12=makeQuery(id+"F0.imprint","IMPRINT",FACE,{"disambiguationData":[TD([[makeQuery(id+"F0.imprint","IMPRINT",EDGE,{"disambiguationData":[TD([[subQ8,-1.0]])],"derivedFrom":subQ3}),-1.0]])]});}
            var Q13;
            {var subQ0=sQuery(id+"F0.wireOp",EDGE,"E16.left");var subQ1=sQuery(id+"F0.wireOp",EDGE,"E1");var subQ2=makeQuery(id+"F0.imprint","INTERSECT",VERTEX,{"derivedFrom":[subQ1,subQ0]});Q13=makeQuery(id+"F0.imprint","IMPRINT",FACE,{"disambiguationData":[TD([[makeQuery(id+"F0.imprint","IMPRINT",EDGE,{"disambiguationData":[TD([[subQ2,-1.0]])],"derivedFrom":subQ1}),1.0]])]});}
            var Q14;
            {var subQ0=sQuery(id+"F0.wireOp",EDGE,"E25");var subQ1=sQuery(id+"F0.wireOp",EDGE,"E1");var subQ2=makeQuery(id+"F0.imprint","INTERSECT",VERTEX,{"disambiguationData":[OD(1.0)],"derivedFrom":[subQ1,subQ0]});Q14=makeQuery(id+"F0.imprint","IMPRINT",FACE,{"disambiguationData":[TD([[makeQuery(id+"F0.imprint","IMPRINT",EDGE,{"disambiguationData":[TD([[subQ2,-1.0]])],"derivedFrom":subQ1}),1.0]])]});}
            var Q15;
            {var subQ0=sQuery(id+"F0.wireOp",EDGE,"E13.MirrorCS");var subQ1=sQuery(id+"F0.wireOp",EDGE,"E1");var subQ2=makeQuery(id+"F0.imprint","INTERSECT",VERTEX,{"derivedFrom":[subQ1,subQ0]});Q15=makeQuery(id+"F0.imprint","IMPRINT",FACE,{"disambiguationData":[TD([[makeQuery(id+"F0.imprint","IMPRINT",EDGE,{"disambiguationData":[TD([[subQ2,-1.0]])],"derivedFrom":subQ1}),1.0]])]});}
            var Q16;
            {var subQ0=sQuery(id+"F0.wireOp",EDGE,"E26");var subQ1=sQuery(id+"F0.wireOp",EDGE,"E1");var subQ2=makeQuery(id+"F0.imprint","INTERSECT",VERTEX,{"disambiguationData":[OD(0.0)],"derivedFrom":[subQ1,subQ0]});Q16=makeQuery(id+"F0.imprint","IMPRINT",FACE,{"disambiguationData":[TD([[makeQuery(id+"F0.imprint","IMPRINT",EDGE,{"disambiguationData":[TD([[subQ2,-1.0]])],"derivedFrom":subQ1}),1.0]])]});}
            var Q17;
            {var subQ0=sQuery(id+"F0.wireOp",EDGE,"E26");var subQ1=sQuery(id+"F0.wireOp",EDGE,"E4");var subQ2=makeQuery(id+"F0.imprint","INTERSECT",VERTEX,{"disambiguationData":[OD(0.0)],"derivedFrom":[subQ1,subQ0]});Q17=makeQuery(id+"F0.imprint","IMPRINT",FACE,{"disambiguationData":[TD([[makeQuery(id+"F0.imprint","IMPRINT",EDGE,{"disambiguationData":[TD([[subQ2,-1.0]])],"derivedFrom":subQ1}),-1.0]])]});}
            var Q18;
            {var subQ0=sQuery(id+"F0.wireOp",EDGE,"E27");var subQ1=sQuery(id+"F0.wireOp",EDGE,"E4");var subQ2=makeQuery(id+"F0.imprint","INTERSECT",VERTEX,{"disambiguationData":[OD(0.0)],"derivedFrom":[subQ1,subQ0]});Q18=makeQuery(id+"F0.imprint","IMPRINT",FACE,{"disambiguationData":[TD([[makeQuery(id+"F0.imprint","IMPRINT",EDGE,{"disambiguationData":[TD([[subQ2,-1.0]])],"derivedFrom":subQ1}),-1.0]])]});}
            var Q19;
            {var subQ5=sQuery(id+"F0.wireOp",EDGE,"E17.left");var subQ7=sQuery(id+"F0.wireOp",EDGE,"E4");var subQ8=makeQuery(id+"F0.imprint","INTERSECT",VERTEX,{"derivedFrom":[subQ7,subQ5]});Q19=makeQuery(id+"F0.imprint","IMPRINT",FACE,{"disambiguationData":[TD([[makeQuery(id+"F0.imprint","IMPRINT",EDGE,{"disambiguationData":[TD([[subQ8,-1.0]])],"derivedFrom":subQ7}),-1.0]])]});}
            var Q20;
            {var subQ0=sQuery(id+"F0.wireOp",EDGE,"E25");var subQ1=sQuery(id+"F0.wireOp",EDGE,"E4");var subQ2=makeQuery(id+"F0.imprint","INTERSECT",VERTEX,{"disambiguationData":[OD(1.0)],"derivedFrom":[subQ1,subQ0]});Q20=makeQuery(id+"F0.imprint","IMPRINT",FACE,{"disambiguationData":[TD([[makeQuery(id+"F0.imprint","IMPRINT",EDGE,{"disambiguationData":[TD([[subQ2,-1.0]])],"derivedFrom":subQ1}),-1.0]])]});}
            var Q21;
            {var subQ0=sQuery(id+"F0.wireOp",EDGE,"E24");var subQ1=sQuery(id+"F0.wireOp",EDGE,"E4");var subQ2=makeQuery(id+"F0.imprint","INTERSECT",VERTEX,{"disambiguationData":[OD(1.0)],"derivedFrom":[subQ1,subQ0]});Q21=makeQuery(id+"F0.imprint","IMPRINT",FACE,{"disambiguationData":[TD([[makeQuery(id+"F0.imprint","IMPRINT",EDGE,{"disambiguationData":[TD([[subQ2,-1.0]])],"derivedFrom":subQ1}),-1.0]])]});}
            var Q22;
            {var subQ0=sQuery(id+"F0.wireOp",EDGE,"E27");var subQ1=sQuery(id+"F0.wireOp",EDGE,"E4");var subQ2=makeQuery(id+"F0.imprint","INTERSECT",VERTEX,{"disambiguationData":[OD(1.0)],"derivedFrom":[subQ1,subQ0]});Q22=makeQuery(id+"F0.imprint","IMPRINT",FACE,{"disambiguationData":[TD([[makeQuery(id+"F0.imprint","IMPRINT",EDGE,{"disambiguationData":[TD([[subQ2,-1.0]])],"derivedFrom":subQ1}),-1.0]])]});}
            var Q23;
            {var subQ0=sQuery(id+"F0.wireOp",EDGE,"E26");var subQ1=sQuery(id+"F0.wireOp",EDGE,"E1");var subQ2=makeQuery(id+"F0.imprint","INTERSECT",VERTEX,{"disambiguationData":[OD(1.0)],"derivedFrom":[subQ1,subQ0]});Q23=makeQuery(id+"F0.imprint","IMPRINT",FACE,{"disambiguationData":[TD([[makeQuery(id+"F0.imprint","IMPRINT",EDGE,{"disambiguationData":[TD([[subQ2,-1.0]])],"derivedFrom":subQ1}),1.0]])]});}
            var Q24;
            {var subQ0=sQuery(id+"F0.wireOp",EDGE,"E5.top");var subQ1=sQuery(id+"F0.wireOp",EDGE,"E1");var subQ2=makeQuery(id+"F0.imprint","INTERSECT",VERTEX,{"derivedFrom":[subQ1,subQ0]});Q24=makeQuery(id+"F0.imprint","IMPRINT",FACE,{"disambiguationData":[TD([[makeQuery(id+"F0.imprint","IMPRINT",EDGE,{"disambiguationData":[TD([[subQ2,-1.0]])],"derivedFrom":subQ1}),1.0]])]});}
            var Q25;
            {var subQ5=sQuery(id+"F0.wireOp",EDGE,"E6.bottom");var subQ7=sQuery(id+"F0.wireOp",EDGE,"E4");var subQ8=makeQuery(id+"F0.imprint","INTERSECT",VERTEX,{"derivedFrom":[subQ7,subQ5]});Q25=makeQuery(id+"F0.imprint","IMPRINT",FACE,{"disambiguationData":[TD([[makeQuery(id+"F0.imprint","IMPRINT",EDGE,{"disambiguationData":[TD([[subQ8,-1.0]])],"derivedFrom":subQ7}),-1.0]])]});}
            var Q26;
            {var subQ0=sQuery(id+"F0.wireOp",EDGE,"E26");var subQ1=sQuery(id+"F0.wireOp",EDGE,"E4");var subQ2=makeQuery(id+"F0.imprint","INTERSECT",VERTEX,{"disambiguationData":[OD(1.0)],"derivedFrom":[subQ1,subQ0]});Q26=makeQuery(id+"F0.imprint","IMPRINT",FACE,{"disambiguationData":[TD([[makeQuery(id+"F0.imprint","IMPRINT",EDGE,{"disambiguationData":[TD([[subQ2,-1.0]])],"derivedFrom":subQ1}),-1.0]])]});}
            var Q27;
            {var subQ0=sQuery(id+"F0.wireOp",EDGE,"E24");var subQ1=sQuery(id+"F0.wireOp",EDGE,"E4");var subQ2=makeQuery(id+"F0.imprint","INTERSECT",VERTEX,{"disambiguationData":[OD(0.0)],"derivedFrom":[subQ1,subQ0]});Q27=makeQuery(id+"F0.imprint","IMPRINT",FACE,{"disambiguationData":[TD([[makeQuery(id+"F0.imprint","IMPRINT",EDGE,{"disambiguationData":[TD([[subQ2,-1.0]])],"derivedFrom":subQ1}),-1.0]])]});}
            var Q28;
            {var subQ0=sQuery(id+"F0.wireOp",EDGE,"E25");var subQ1=sQuery(id+"F0.wireOp",EDGE,"E4");var subQ2=makeQuery(id+"F0.imprint","INTERSECT",VERTEX,{"disambiguationData":[OD(0.0)],"derivedFrom":[subQ1,subQ0]});Q28=makeQuery(id+"F0.imprint","IMPRINT",FACE,{"disambiguationData":[TD([[makeQuery(id+"F0.imprint","IMPRINT",EDGE,{"disambiguationData":[TD([[subQ2,-1.0]])],"derivedFrom":subQ1}),-1.0]])]});}
            var Q29;
            {var subQ0=sQuery(id+"F0.wireOp",EDGE,"E25");var subQ1=sQuery(id+"F0.wireOp",EDGE,"E1");var subQ2=makeQuery(id+"F0.imprint","INTERSECT",VERTEX,{"disambiguationData":[OD(0.0)],"derivedFrom":[subQ1,subQ0]});Q29=makeQuery(id+"F0.imprint","IMPRINT",FACE,{"disambiguationData":[TD([[makeQuery(id+"F0.imprint","IMPRINT",EDGE,{"disambiguationData":[TD([[subQ2,-1.0]])],"derivedFrom":subQ1}),1.0]])]});}
            var Q30;
            {var subQ0=sQuery(id+"F0.wireOp",EDGE,"E19.right");var subQ1=sQuery(id+"F0.wireOp",EDGE,"E1");var subQ2=makeQuery(id+"F0.imprint","INTERSECT",VERTEX,{"derivedFrom":[subQ1,subQ0]});Q30=makeQuery(id+"F0.imprint","IMPRINT",FACE,{"disambiguationData":[TD([[makeQuery(id+"F0.imprint","IMPRINT",EDGE,{"disambiguationData":[TD([[subQ2,-1.0]])],"derivedFrom":subQ1}),1.0]])]});}
            var Q31;
            {var subQ5=sQuery(id+"F0.wireOp",EDGE,"E20.right");var subQ7=sQuery(id+"F0.wireOp",EDGE,"E4");var subQ8=makeQuery(id+"F0.imprint","INTERSECT",VERTEX,{"derivedFrom":[subQ7,subQ5]});Q31=makeQuery(id+"F0.imprint","IMPRINT",FACE,{"disambiguationData":[TD([[makeQuery(id+"F0.imprint","IMPRINT",EDGE,{"disambiguationData":[TD([[subQ8,-1.0]])],"derivedFrom":subQ7}),-1.0]])]});}
            var Q32;
            {var subQ5=sQuery(id+"F0.wireOp",EDGE,"E15.MirrorCS");var subQ7=sQuery(id+"F0.wireOp",EDGE,"E4");var subQ8=makeQuery(id+"F0.imprint","INTERSECT",VERTEX,{"derivedFrom":[subQ7,subQ5]});Q32=makeQuery(id+"F0.imprint","IMPRINT",FACE,{"disambiguationData":[TD([[makeQuery(id+"F0.imprint","IMPRINT",EDGE,{"disambiguationData":[TD([[subQ8,-1.0]])],"derivedFrom":subQ7}),-1.0]])]});}
            extrude(context, id + "F2", {"entities" : qUnion([Q0, Q1, Q2, Q3, Q4, Q5, Q6, Q7, Q8, Q9, Q10, Q11, Q12, Q13, Q14, Q15, Q16, Q17, Q18, Q19, Q20, Q21, Q22, Q23, Q24, Q25, Q26, Q27, Q28, Q29, Q30, Q31, Q32]), "operationType" : NewBodyOperationType.ADD, "oppositeDirection" : true, "depth" : 6 * mm, "offsetDistance" : 25 * mm});
        }
        {
            var Q0;
            {var subQ5=sQuery(id+"F0.wireOp",EDGE,"E1");var subQ7=sQuery(id+"F0.wireOp",EDGE,"E7");var subQ8=makeQuery(id+"F0.imprint","INTERSECT",VERTEX,{"disambiguationData":[OD(0.0)],"derivedFrom":[subQ5,subQ7]});Q0=makeQuery(id+"F0.imprint","IMPRINT",FACE,{"disambiguationData":[TD([[makeQuery(id+"F0.imprint","IMPRINT",EDGE,{"disambiguationData":[TD([[subQ8,1.0]])],"derivedFrom":subQ5}),1.0]])]});}
            var Q1;
            {var subQ0=sQuery(id+"F0.wireOp",EDGE,"E7");var subQ1=sQuery(id+"F0.wireOp",EDGE,"E1");var subQ2=makeQuery(id+"F0.imprint","INTERSECT",VERTEX,{"disambiguationData":[OD(1.0)],"derivedFrom":[subQ1,subQ0]});Q1=makeQuery(id+"F0.imprint","IMPRINT",FACE,{"disambiguationData":[TD([[makeQuery(id+"F0.imprint","IMPRINT",EDGE,{"disambiguationData":[TD([[subQ2,1.0]])],"derivedFrom":subQ1}),1.0]])]});}
            var Q2;
            {var subQ3=sQuery(id+"F0.wireOp",EDGE,"E18");var subQ7=sQuery(id+"F0.wireOp",EDGE,"E1");var subQ9=makeQuery(id+"F0.imprint","INTERSECT",VERTEX,{"disambiguationData":[OD(1.0)],"derivedFrom":[subQ7,subQ3]});Q2=makeQuery(id+"F0.imprint","IMPRINT",FACE,{"disambiguationData":[TD([[makeQuery(id+"F0.imprint","IMPRINT",EDGE,{"disambiguationData":[TD([[subQ9,1.0]])],"derivedFrom":subQ7}),1.0]])]});}
            var Q3;
            {var subQ5=sQuery(id+"F0.wireOp",EDGE,"E1");var subQ7=sQuery(id+"F0.wireOp",EDGE,"E18");var subQ8=makeQuery(id+"F0.imprint","INTERSECT",VERTEX,{"disambiguationData":[OD(0.0)],"derivedFrom":[subQ5,subQ7]});Q3=makeQuery(id+"F0.imprint","IMPRINT",FACE,{"disambiguationData":[TD([[makeQuery(id+"F0.imprint","IMPRINT",EDGE,{"disambiguationData":[TD([[subQ8,1.0]])],"derivedFrom":subQ5}),1.0]])]});}
            var Q4;
            {var subQ0=sQuery(id+"F0.wireOp",EDGE,"E25");var subQ1=sQuery(id+"F0.wireOp",EDGE,"E1");var subQ2=makeQuery(id+"F0.imprint","INTERSECT",VERTEX,{"disambiguationData":[OD(0.0)],"derivedFrom":[subQ1,subQ0]});Q4=makeQuery(id+"F0.imprint","IMPRINT",FACE,{"disambiguationData":[TD([[makeQuery(id+"F0.imprint","IMPRINT",EDGE,{"disambiguationData":[TD([[subQ2,-1.0]])],"derivedFrom":subQ1}),1.0]])]});}
            var Q5;
            {var subQ0=sQuery(id+"F0.wireOp",EDGE,"E19.right");var subQ1=sQuery(id+"F0.wireOp",EDGE,"E1");var subQ2=makeQuery(id+"F0.imprint","INTERSECT",VERTEX,{"derivedFrom":[subQ1,subQ0]});Q5=makeQuery(id+"F0.imprint","IMPRINT",FACE,{"disambiguationData":[TD([[makeQuery(id+"F0.imprint","IMPRINT",EDGE,{"disambiguationData":[TD([[subQ2,-1.0]])],"derivedFrom":subQ1}),1.0]])]});}
            var Q6;
            {var subQ0=sQuery(id+"F0.wireOp",EDGE,"E26");var subQ1=sQuery(id+"F0.wireOp",EDGE,"E1");var subQ2=makeQuery(id+"F0.imprint","INTERSECT",VERTEX,{"disambiguationData":[OD(0.0)],"derivedFrom":[subQ1,subQ0]});Q6=makeQuery(id+"F0.imprint","IMPRINT",FACE,{"disambiguationData":[TD([[makeQuery(id+"F0.imprint","IMPRINT",EDGE,{"disambiguationData":[TD([[subQ2,-1.0]])],"derivedFrom":subQ1}),1.0]])]});}
            var Q7;
            {var subQ0=sQuery(id+"F0.wireOp",EDGE,"E13.MirrorCS");var subQ1=sQuery(id+"F0.wireOp",EDGE,"E1");var subQ2=makeQuery(id+"F0.imprint","INTERSECT",VERTEX,{"derivedFrom":[subQ1,subQ0]});Q7=makeQuery(id+"F0.imprint","IMPRINT",FACE,{"disambiguationData":[TD([[makeQuery(id+"F0.imprint","IMPRINT",EDGE,{"disambiguationData":[TD([[subQ2,-1.0]])],"derivedFrom":subQ1}),1.0]])]});}
            var Q8;
            {var subQ0=sQuery(id+"F0.wireOp",EDGE,"E25");var subQ1=sQuery(id+"F0.wireOp",EDGE,"E1");var subQ2=makeQuery(id+"F0.imprint","INTERSECT",VERTEX,{"disambiguationData":[OD(1.0)],"derivedFrom":[subQ1,subQ0]});Q8=makeQuery(id+"F0.imprint","IMPRINT",FACE,{"disambiguationData":[TD([[makeQuery(id+"F0.imprint","IMPRINT",EDGE,{"disambiguationData":[TD([[subQ2,-1.0]])],"derivedFrom":subQ1}),1.0]])]});}
            var Q9;
            {var subQ0=sQuery(id+"F0.wireOp",EDGE,"E16.left");var subQ1=sQuery(id+"F0.wireOp",EDGE,"E1");var subQ2=makeQuery(id+"F0.imprint","INTERSECT",VERTEX,{"derivedFrom":[subQ1,subQ0]});Q9=makeQuery(id+"F0.imprint","IMPRINT",FACE,{"disambiguationData":[TD([[makeQuery(id+"F0.imprint","IMPRINT",EDGE,{"disambiguationData":[TD([[subQ2,-1.0]])],"derivedFrom":subQ1}),1.0]])]});}
            var Q10;
            {var subQ0=sQuery(id+"F0.wireOp",EDGE,"E26");var subQ1=sQuery(id+"F0.wireOp",EDGE,"E1");var subQ2=makeQuery(id+"F0.imprint","INTERSECT",VERTEX,{"disambiguationData":[OD(1.0)],"derivedFrom":[subQ1,subQ0]});Q10=makeQuery(id+"F0.imprint","IMPRINT",FACE,{"disambiguationData":[TD([[makeQuery(id+"F0.imprint","IMPRINT",EDGE,{"disambiguationData":[TD([[subQ2,-1.0]])],"derivedFrom":subQ1}),1.0]])]});}
            var Q11;
            {var subQ0=sQuery(id+"F0.wireOp",EDGE,"E5.top");var subQ1=sQuery(id+"F0.wireOp",EDGE,"E1");var subQ2=makeQuery(id+"F0.imprint","INTERSECT",VERTEX,{"derivedFrom":[subQ1,subQ0]});Q11=makeQuery(id+"F0.imprint","IMPRINT",FACE,{"disambiguationData":[TD([[makeQuery(id+"F0.imprint","IMPRINT",EDGE,{"disambiguationData":[TD([[subQ2,-1.0]])],"derivedFrom":subQ1}),1.0]])]});}
            extrude(context, id + "F3", {"entities" : qUnion([Q0, Q1, Q2, Q3, Q4, Q5, Q6, Q7, Q8, Q9, Q10, Q11]), "operationType" : NewBodyOperationType.REMOVE, "oppositeDirection" : true, "depth" : 4 * mm, "offsetDistance" : 25 * mm});
        }
        {
            var Q0;
            {var subQ0=sQuery(id+"F0.wireOp",EDGE,"E7");var subQ1=sQuery(id+"F0.wireOp",EDGE,"E0");var subQ2=makeQuery(id+"F0.imprint","INTERSECT",VERTEX,{"disambiguationData":[OD(0.0)],"derivedFrom":[subQ1,subQ0]});Q0=makeQuery(id+"F0.imprint","IMPRINT",FACE,{"disambiguationData":[TD([[makeQuery(id+"F0.imprint","IMPRINT",EDGE,{"disambiguationData":[TD([[subQ2,1.0]])],"derivedFrom":subQ1}),1.0]])]});}
            var Q1;
            {var subQ0=sQuery(id+"F0.wireOp",EDGE,"E7");var subQ1=sQuery(id+"F0.wireOp",EDGE,"E0");var subQ2=makeQuery(id+"F0.imprint","INTERSECT",VERTEX,{"disambiguationData":[OD(1.0)],"derivedFrom":[subQ1,subQ0]});Q1=makeQuery(id+"F0.imprint","IMPRINT",FACE,{"disambiguationData":[TD([[makeQuery(id+"F0.imprint","IMPRINT",EDGE,{"disambiguationData":[TD([[subQ2,1.0]])],"derivedFrom":subQ1}),1.0]])]});}
            var Q2;
            {var subQ0=sQuery(id+"F0.wireOp",EDGE,"E18");var subQ1=sQuery(id+"F0.wireOp",EDGE,"E0");var subQ2=makeQuery(id+"F0.imprint","INTERSECT",VERTEX,{"disambiguationData":[OD(0.0)],"derivedFrom":[subQ1,subQ0]});Q2=makeQuery(id+"F0.imprint","IMPRINT",FACE,{"disambiguationData":[TD([[makeQuery(id+"F0.imprint","IMPRINT",EDGE,{"disambiguationData":[TD([[subQ2,1.0]])],"derivedFrom":subQ1}),1.0]])]});}
            var Q3;
            {var subQ0=sQuery(id+"F0.wireOp",EDGE,"E18");var subQ1=sQuery(id+"F0.wireOp",EDGE,"E0");var subQ2=makeQuery(id+"F0.imprint","INTERSECT",VERTEX,{"disambiguationData":[OD(1.0)],"derivedFrom":[subQ1,subQ0]});Q3=makeQuery(id+"F0.imprint","IMPRINT",FACE,{"disambiguationData":[TD([[makeQuery(id+"F0.imprint","IMPRINT",EDGE,{"disambiguationData":[TD([[subQ2,1.0]])],"derivedFrom":subQ1}),1.0]])]});}
            extrude(context, id + "F4", {"entities" : qUnion([Q0, Q1, Q2, Q3]), "operationType" : NewBodyOperationType.REMOVE, "endBound" : BoundingType.UP_TO_NEXT, "oppositeDirection" : true, "depth" : 25 * mm, "offsetDistance" : 25 * mm});
        }
        {
            var Q0;
            {var subQ0=sQuery(id+"F0.wireOp",EDGE,"E7");var subQ1=sQuery(id+"F0.wireOp",EDGE,"E0");var subQ2=sQuery(id+"F0.wireOp",EDGE,"E3");Q0=makeQuery(id+"F4.boolean.opBoolean","SPLIT",FACE,{"disambiguationData":[TD([makeQuery(id+"F4.opExtrude","SWEPT_FACE",FACE,{"disambiguationData":[OSD([subQ0]),TDD([makeQuery(id+"F0.imprint","IMPRINT",EDGE,{"disambiguationData":[TD([[makeQuery(id+"F0.imprint","INTERSECT",VERTEX,{"disambiguationData":[OD(0.0)],"derivedFrom":[subQ1,subQ0]}),-1.0]])],"derivedFrom":subQ0})])]})])],"derivedFrom":makeQuery(id+"F2.opExtrude","CAP_FACE",FACE,{"disambiguationData":[OSD([subQ1,subQ2])],"isStart":false})});}
            var Q1;
            {var subQ0=sQuery(id+"F0.wireOp",EDGE,"E18");var subQ1=sQuery(id+"F0.wireOp",EDGE,"E0");var subQ2=sQuery(id+"F0.wireOp",EDGE,"E3");Q1=makeQuery(id+"F4.boolean.opBoolean","SPLIT",FACE,{"disambiguationData":[TD([makeQuery(id+"F4.opExtrude","SWEPT_FACE",FACE,{"disambiguationData":[OSD([subQ0]),TDD([makeQuery(id+"F0.imprint","IMPRINT",EDGE,{"disambiguationData":[TD([[makeQuery(id+"F0.imprint","INTERSECT",VERTEX,{"disambiguationData":[OD(1.0)],"derivedFrom":[subQ1,subQ0]}),1.0]])],"derivedFrom":subQ0})])]})])],"derivedFrom":makeQuery(id+"F2.opExtrude","CAP_FACE",FACE,{"disambiguationData":[OSD([subQ1,subQ2])],"isStart":false})});}
            var Q2;
            {var subQ0=sQuery(id+"F0.wireOp",EDGE,"E7");var subQ1=sQuery(id+"F0.wireOp",EDGE,"E0");var subQ2=sQuery(id+"F0.wireOp",EDGE,"E3");Q2=makeQuery(id+"F4.boolean.opBoolean","SPLIT",FACE,{"disambiguationData":[TD([makeQuery(id+"F4.opExtrude","SWEPT_FACE",FACE,{"disambiguationData":[OSD([subQ0]),TDD([makeQuery(id+"F0.imprint","IMPRINT",EDGE,{"disambiguationData":[TD([[makeQuery(id+"F0.imprint","INTERSECT",VERTEX,{"disambiguationData":[OD(1.0)],"derivedFrom":[subQ1,subQ0]}),1.0]])],"derivedFrom":subQ0})])]})])],"derivedFrom":makeQuery(id+"F2.opExtrude","CAP_FACE",FACE,{"disambiguationData":[OSD([subQ1,subQ2])],"isStart":false})});}
            var Q3;
            {var subQ0=sQuery(id+"F0.wireOp",EDGE,"E18");var subQ1=sQuery(id+"F0.wireOp",EDGE,"E0");var subQ2=sQuery(id+"F0.wireOp",EDGE,"E3");Q3=makeQuery(id+"F4.boolean.opBoolean","SPLIT",FACE,{"disambiguationData":[TD([makeQuery(id+"F4.opExtrude","SWEPT_FACE",FACE,{"disambiguationData":[OSD([subQ0]),TDD([makeQuery(id+"F0.imprint","IMPRINT",EDGE,{"disambiguationData":[TD([[makeQuery(id+"F0.imprint","INTERSECT",VERTEX,{"disambiguationData":[OD(0.0)],"derivedFrom":[subQ1,subQ0]}),-1.0]])],"derivedFrom":subQ0})])]})])],"derivedFrom":makeQuery(id+"F2.opExtrude","CAP_FACE",FACE,{"disambiguationData":[OSD([subQ1,subQ2])],"isStart":false})});}
            var Q4;
            Q4=makeQuery(id+"F2.opExtrude","CAP_FACE",FACE,{"disambiguationData":[OSD([sQuery(id+"F0.wireOp",EDGE,"E1"),sQuery(id+"F0.wireOp",EDGE,"E4"),sQuery(id+"F0.wireOp",EDGE,"E10.MirrorCS"),sQuery(id+"F0.wireOp",EDGE,"E11.MirrorCS"),sQuery(id+"F0.wireOp",EDGE,"E16.left"),sQuery(id+"F0.wireOp",EDGE,"E17.left")])],"isStart":false});
            var Q5;
            Q5=makeQuery(id+"F2.opExtrude","CAP_FACE",FACE,{"disambiguationData":[OSD([sQuery(id+"F0.wireOp",EDGE,"E1"),sQuery(id+"F0.wireOp",EDGE,"E4"),sQuery(id+"F0.wireOp",EDGE,"E13.MirrorCS"),sQuery(id+"F0.wireOp",EDGE,"E15.MirrorCS"),sQuery(id+"F0.wireOp",EDGE,"E19.left"),sQuery(id+"F0.wireOp",EDGE,"E20.left")])],"isStart":false});
            var Q6;
            Q6=makeQuery(id+"F2.opExtrude","CAP_FACE",FACE,{"disambiguationData":[OSD([sQuery(id+"F0.wireOp",EDGE,"E1"),sQuery(id+"F0.wireOp",EDGE,"E4"),sQuery(id+"F0.wireOp",EDGE,"E5.bottom"),sQuery(id+"F0.wireOp",EDGE,"E6.top"),sQuery(id+"F0.wireOp",EDGE,"E19.right"),sQuery(id+"F0.wireOp",EDGE,"E20.right")])],"isStart":false});
            var Q7;
            Q7=makeQuery(id+"F2.opExtrude","CAP_FACE",FACE,{"disambiguationData":[OSD([sQuery(id+"F0.wireOp",EDGE,"E1"),sQuery(id+"F0.wireOp",EDGE,"E4"),sQuery(id+"F0.wireOp",EDGE,"E5.top"),sQuery(id+"F0.wireOp",EDGE,"E6.bottom"),sQuery(id+"F0.wireOp",EDGE,"E16.right"),sQuery(id+"F0.wireOp",EDGE,"E17.right")])],"isStart":false});
            var Q8;
            {var subQ0=sQuery(id+"F0.wireOp",EDGE,"E25");var subQ1=sQuery(id+"F0.wireOp",EDGE,"E0");var subQ2=sQuery(id+"F0.wireOp",EDGE,"E3");Q8=makeQuery(id+"F4.boolean.opBoolean","SPLIT",FACE,{"disambiguationData":[TD([makeQuery(id+"F4.opExtrude","SWEPT_FACE",FACE,{"disambiguationData":[OSD([subQ0]),TDD([makeQuery(id+"F0.imprint","IMPRINT",EDGE,{"disambiguationData":[TD([[makeQuery(id+"F0.imprint","INTERSECT",VERTEX,{"disambiguationData":[OD(1.0)],"derivedFrom":[subQ1,subQ0]}),1.0]])],"derivedFrom":subQ0})])]})])],"derivedFrom":makeQuery(id+"F2.opExtrude","CAP_FACE",FACE,{"disambiguationData":[OSD([subQ1,subQ2])],"isStart":false})});}
            fillet(context, id + "F5", {"entities" : qUnion([Q0, Q1, Q2, Q3, Q4, Q5, Q6, Q7, Q8]), "radius" : 0.5 * mm, "tangentPropagation" : true, "allowEdgeOverflow" : false});
        }
        {
            var Q0;
            Q0=makeQuery(id+"F3.boolean.opBoolean","COPY",FACE,{"derivedFrom":makeQuery(id+"F3.opExtrude","CAP_FACE",FACE,{"disambiguationData":[OSD([sQuery(id+"F0.wireOp",EDGE,"E1"),sQuery(id+"F0.wireOp",EDGE,"E5.top"),sQuery(id+"F0.wireOp",EDGE,"E7"),sQuery(id+"F0.wireOp",EDGE,"E21")])],"isStart":false})});
            var sketch = newSketch(context, id + "F6", { "sketchPlane" : qUnion([Q0])});
            skCircle(sketch, "E28.0", {"center": v(0, 0) * mm, "radius": 35 * mm});
            skCircle(sketch, "E28.1", {"center": v(0, 0) * mm, "radius": 29.5 * mm});
            skCircle(sketch, "E28.2", {"center": v(0, 0) * mm, "radius": 31 * mm});
            skCircle(sketch, "E28.3", {"center": v(0, 0) * mm, "radius": 33.5 * mm});
            skCircle(sketch, "E28.4", {"center": v(0, 0) * mm, "radius": 22.5 * mm});
            skLineSegment(sketch, "E28.5", {"start": v(-22.5, 3) * mm, "end": v(-29.5, 3) * mm});
            skLineSegment(sketch, "E28.6", {"start": v(-22.5, -3) * mm, "end": v(-29.5, -3) * mm});
            skLineSegment(sketch, "E28.7", {"start": v(-22.5, 3) * mm, "end": v(-22.5, -3) * mm});
            skLineSegment(sketch, "E28.8", {"start": v(-29.5, 3) * mm, "end": v(-29.5, -3) * mm});
            skPoint(sketch, "E28.9", {"position": v(-26, 0) * mm});
            skLineSegment(sketch, "E28.10", {"start": v(-22.5, -3) * mm, "end": v(-21.5, -3) * mm});
            skLineSegment(sketch, "E28.11", {"start": v(-22.5, 3) * mm, "end": v(-21.5, 3) * mm});
            skLineSegment(sketch, "E28.12", {"start": v(-22.5, -3) * mm, "end": v(-22.5, 3) * mm});
            skLineSegment(sketch, "E28.13", {"start": v(-21.5, -3) * mm, "end": v(-21.5, 3) * mm});
            skPoint(sketch, "E28.14", {"position": v(-22, 0) * mm});
            skLineSegment(sketch, "E28.15", {"start": v(-30.31, -17.5) * mm, "end": v(30.31, 17.5) * mm});
            skLineSegment(sketch, "E28.16", {"start": v(0, -35) * mm, "end": v(0, 35) * mm});
            skLineSegment(sketch, "E28.17", {"start": v(21.5, -3) * mm, "end": v(21.5, 3) * mm});
            skLineSegment(sketch, "E28.18", {"start": v(22.5, -3) * mm, "end": v(21.5, -3) * mm});
            skLineSegment(sketch, "E28.19", {"start": v(22.5, -3) * mm, "end": v(29.5, -3) * mm});
            skLineSegment(sketch, "E28.20", {"start": v(29.5, 3) * mm, "end": v(29.5, -3) * mm});
            skLineSegment(sketch, "E28.21", {"start": v(22.5, 3) * mm, "end": v(29.5, 3) * mm});
            skLineSegment(sketch, "E28.22", {"start": v(22.5, -3) * mm, "end": v(22.5, 3) * mm});
            skLineSegment(sketch, "E28.23", {"start": v(22.5, 3) * mm, "end": v(21.5, 3) * mm});
            skLineSegment(sketch, "E28.24", {"start": v(3, -22.5) * mm, "end": v(-3, -22.5) * mm});
            skLineSegment(sketch, "E28.25", {"start": v(3, -29.5) * mm, "end": v(-3, -29.5) * mm});
            skLineSegment(sketch, "E28.26", {"start": v(3, -22.5) * mm, "end": v(3, -29.5) * mm});
            skLineSegment(sketch, "E28.27", {"start": v(-3, -22.5) * mm, "end": v(-3, -29.5) * mm});
            skPoint(sketch, "E28.28", {"position": v(0, -26) * mm});
            skLineSegment(sketch, "E28.29", {"start": v(3, -21.5) * mm, "end": v(-3, -21.5) * mm});
            skLineSegment(sketch, "E28.30", {"start": v(3, -22.5) * mm, "end": v(-3, -22.5) * mm});
            skLineSegment(sketch, "E28.31", {"start": v(3, -21.5) * mm, "end": v(3, -22.5) * mm});
            skLineSegment(sketch, "E28.32", {"start": v(-3, -21.5) * mm, "end": v(-3, -22.5) * mm});
            skPoint(sketch, "E28.33", {"position": v(0, -22) * mm});
            skLineSegment(sketch, "E28.34", {"start": v(17.5, -30.31) * mm, "end": v(-17.5, 30.31) * mm});
            skLineSegment(sketch, "E28.35", {"start": v(3, 22.5) * mm, "end": v(-3, 22.5) * mm});
            skLineSegment(sketch, "E28.36", {"start": v(3, 29.5) * mm, "end": v(-3, 29.5) * mm});
            skLineSegment(sketch, "E28.37", {"start": v(3, 22.5) * mm, "end": v(3, 29.5) * mm});
            skLineSegment(sketch, "E28.38", {"start": v(-3, 22.5) * mm, "end": v(-3, 29.5) * mm});
            skPoint(sketch, "E28.39", {"position": v(0, 26) * mm});
            skLineSegment(sketch, "E28.40", {"start": v(3, 21.5) * mm, "end": v(-3, 21.5) * mm});
            skLineSegment(sketch, "E28.41", {"start": v(3, 22.5) * mm, "end": v(-3, 22.5) * mm});
            skLineSegment(sketch, "E28.42", {"start": v(3, 21.5) * mm, "end": v(3, 22.5) * mm});
            skLineSegment(sketch, "E28.43", {"start": v(-3, 21.5) * mm, "end": v(-3, 22.5) * mm});
            skPoint(sketch, "E28.44", {"position": v(0, 22) * mm});
            skPoint(sketch, "E28.45", {"position": v(0, 29.5) * mm});
            skPoint(sketch, "E28.46", {"position": v(0, 29.5) * mm});
            skCircle(sketch, "E28.47", {"center": v(0, 0) * mm, "radius": 25 * mm});
            skLineSegment(sketch, "E28.48", {"start": v(-35, 0) * mm, "end": v(35, 0) * mm});
            skPoint(sketch, "E28.49", {"position": v(3, -22) * mm});
            skLineSegment(sketch, "E28.50", {"start": v(9.06, -33.8) * mm, "end": v(-9.06, 33.8) * mm});
            skLineSegment(sketch, "E28.51", {"start": v(7.28, -34.24) * mm, "end": v(-7.28, 34.24) * mm});
            skLineSegment(sketch, "E28.52", {"start": v(-34.24, -7.28) * mm, "end": v(34.24, 7.28) * mm});
            skLineSegment(sketch, "E28.53", {"start": v(-33.8, -9.06) * mm, "end": v(33.8, 9.06) * mm});
            skCircle(sketch, "E28.54.0", {"center": v(0, 0) * mm, "radius": 35 * mm});
            skSolve(sketch);
        }
        {
            var Q0;
            {var subQ0=sQuery(id+"F6.wireOp",EDGE,"E28.51");var subQ1=sQuery(id+"F6.wireOp",EDGE,"E28.1");var subQ2=makeQuery(id+"F6.imprint","INTERSECT",VERTEX,{"disambiguationData":[OD(0.0)],"derivedFrom":[subQ1,subQ0]});Q0=makeQuery(id+"F6.imprint","IMPRINT",FACE,{"disambiguationData":[TD([[makeQuery(id+"F6.imprint","IMPRINT",EDGE,{"disambiguationData":[TD([[subQ2,-1.0]])],"derivedFrom":subQ1}),1.0]])]});}
            var Q1;
            {var subQ0=sQuery(id+"F6.wireOp",EDGE,"E28.52");var subQ1=sQuery(id+"F6.wireOp",EDGE,"E28.1");var subQ2=makeQuery(id+"F6.imprint","INTERSECT",VERTEX,{"disambiguationData":[OD(0.0)],"derivedFrom":[subQ1,subQ0]});Q1=makeQuery(id+"F6.imprint","IMPRINT",FACE,{"disambiguationData":[TD([[makeQuery(id+"F6.imprint","IMPRINT",EDGE,{"disambiguationData":[TD([[subQ2,-1.0]])],"derivedFrom":subQ1}),1.0]])]});}
            var Q2;
            {var subQ0=sQuery(id+"F6.wireOp",EDGE,"E28.51");var subQ1=sQuery(id+"F6.wireOp",EDGE,"E28.1");var subQ2=makeQuery(id+"F6.imprint","INTERSECT",VERTEX,{"disambiguationData":[OD(1.0)],"derivedFrom":[subQ1,subQ0]});Q2=makeQuery(id+"F6.imprint","IMPRINT",FACE,{"disambiguationData":[TD([[makeQuery(id+"F6.imprint","IMPRINT",EDGE,{"disambiguationData":[TD([[subQ2,-1.0]])],"derivedFrom":subQ1}),1.0]])]});}
            var Q3;
            {var subQ0=sQuery(id+"F6.wireOp",EDGE,"E28.52");var subQ1=sQuery(id+"F6.wireOp",EDGE,"E28.1");var subQ2=makeQuery(id+"F6.imprint","INTERSECT",VERTEX,{"disambiguationData":[OD(1.0)],"derivedFrom":[subQ1,subQ0]});Q3=makeQuery(id+"F6.imprint","IMPRINT",FACE,{"disambiguationData":[TD([[makeQuery(id+"F6.imprint","IMPRINT",EDGE,{"disambiguationData":[TD([[subQ2,-1.0]])],"derivedFrom":subQ1}),1.0]])]});}
            extrude(context, id + "F7", {"entities" : qUnion([Q0, Q1, Q2, Q3]), "operationType" : NewBodyOperationType.ADD, "depth" : 1 * mm, "offsetDistance" : 25 * mm});
        }
        {
            var Q0;
            {var subQ0=sQuery(id+"F6.wireOp",EDGE,"E28.51");Q0=makeQuery(id+"F7.opExtrude","CAP_EDGE",EDGE,{"disambiguationData":[OSD([subQ0]),TDD([makeQuery(id+"F6.imprint","IMPRINT",EDGE,{"disambiguationData":[TD([[makeQuery(id+"F6.imprint","INTERSECT",VERTEX,{"disambiguationData":[OD(0.0)],"derivedFrom":[sQuery(id+"F6.wireOp",EDGE,"E28.1"),subQ0]}),1.0]])],"derivedFrom":subQ0})])],"isStart":false});}
            var Q1;
            {var subQ0=sQuery(id+"F6.wireOp",EDGE,"E28.50");Q1=makeQuery(id+"F7.opExtrude","CAP_EDGE",EDGE,{"disambiguationData":[OSD([subQ0]),TDD([makeQuery(id+"F6.imprint","IMPRINT",EDGE,{"disambiguationData":[TD([[makeQuery(id+"F6.imprint","INTERSECT",VERTEX,{"disambiguationData":[OD(0.0)],"derivedFrom":[sQuery(id+"F6.wireOp",EDGE,"E28.1"),subQ0]}),1.0]])],"derivedFrom":subQ0})])],"isStart":true});}
            var Q2;
            {var subQ0=sQuery(id+"F6.wireOp",EDGE,"E28.53");Q2=makeQuery(id+"F7.opExtrude","CAP_EDGE",EDGE,{"disambiguationData":[OSD([subQ0]),TDD([makeQuery(id+"F6.imprint","IMPRINT",EDGE,{"disambiguationData":[TD([[makeQuery(id+"F6.imprint","INTERSECT",VERTEX,{"disambiguationData":[OD(0.0)],"derivedFrom":[sQuery(id+"F6.wireOp",EDGE,"E28.1"),subQ0]}),1.0]])],"derivedFrom":subQ0})])],"isStart":true});}
            var Q3;
            {var subQ0=sQuery(id+"F6.wireOp",EDGE,"E28.52");Q3=makeQuery(id+"F7.opExtrude","CAP_EDGE",EDGE,{"disambiguationData":[OSD([subQ0]),TDD([makeQuery(id+"F6.imprint","IMPRINT",EDGE,{"disambiguationData":[TD([[makeQuery(id+"F6.imprint","INTERSECT",VERTEX,{"disambiguationData":[OD(0.0)],"derivedFrom":[sQuery(id+"F6.wireOp",EDGE,"E28.1"),subQ0]}),1.0]])],"derivedFrom":subQ0})])],"isStart":false});}
            var Q4;
            {var subQ0=sQuery(id+"F6.wireOp",EDGE,"E28.51");Q4=makeQuery(id+"F7.opExtrude","CAP_EDGE",EDGE,{"disambiguationData":[OSD([subQ0]),TDD([makeQuery(id+"F6.imprint","IMPRINT",EDGE,{"disambiguationData":[TD([[makeQuery(id+"F6.imprint","INTERSECT",VERTEX,{"disambiguationData":[OD(1.0)],"derivedFrom":[sQuery(id+"F6.wireOp",EDGE,"E28.1"),subQ0]}),-1.0]])],"derivedFrom":subQ0})])],"isStart":false});}
            var Q5;
            {var subQ0=sQuery(id+"F6.wireOp",EDGE,"E28.50");Q5=makeQuery(id+"F7.opExtrude","CAP_EDGE",EDGE,{"disambiguationData":[OSD([subQ0]),TDD([makeQuery(id+"F6.imprint","IMPRINT",EDGE,{"disambiguationData":[TD([[makeQuery(id+"F6.imprint","INTERSECT",VERTEX,{"disambiguationData":[OD(1.0)],"derivedFrom":[sQuery(id+"F6.wireOp",EDGE,"E28.1"),subQ0]}),-1.0]])],"derivedFrom":subQ0})])],"isStart":true});}
            var Q6;
            {var subQ0=sQuery(id+"F6.wireOp",EDGE,"E28.52");Q6=makeQuery(id+"F7.opExtrude","CAP_EDGE",EDGE,{"disambiguationData":[OSD([subQ0]),TDD([makeQuery(id+"F6.imprint","IMPRINT",EDGE,{"disambiguationData":[TD([[makeQuery(id+"F6.imprint","INTERSECT",VERTEX,{"disambiguationData":[OD(1.0)],"derivedFrom":[sQuery(id+"F6.wireOp",EDGE,"E28.1"),subQ0]}),-1.0]])],"derivedFrom":subQ0})])],"isStart":false});}
            var Q7;
            {var subQ0=sQuery(id+"F6.wireOp",EDGE,"E28.53");Q7=makeQuery(id+"F7.opExtrude","CAP_EDGE",EDGE,{"disambiguationData":[OSD([subQ0]),TDD([makeQuery(id+"F6.imprint","IMPRINT",EDGE,{"disambiguationData":[TD([[makeQuery(id+"F6.imprint","INTERSECT",VERTEX,{"disambiguationData":[OD(1.0)],"derivedFrom":[sQuery(id+"F6.wireOp",EDGE,"E28.1"),subQ0]}),-1.0]])],"derivedFrom":subQ0})])],"isStart":true});}
            fillet(context, id + "F8", {"entities" : qUnion([Q0, Q1, Q2, Q3, Q4, Q5, Q6, Q7]), "radius" : 1 * mm, "tangentPropagation" : true, "allowEdgeOverflow" : false});
        }
    });
